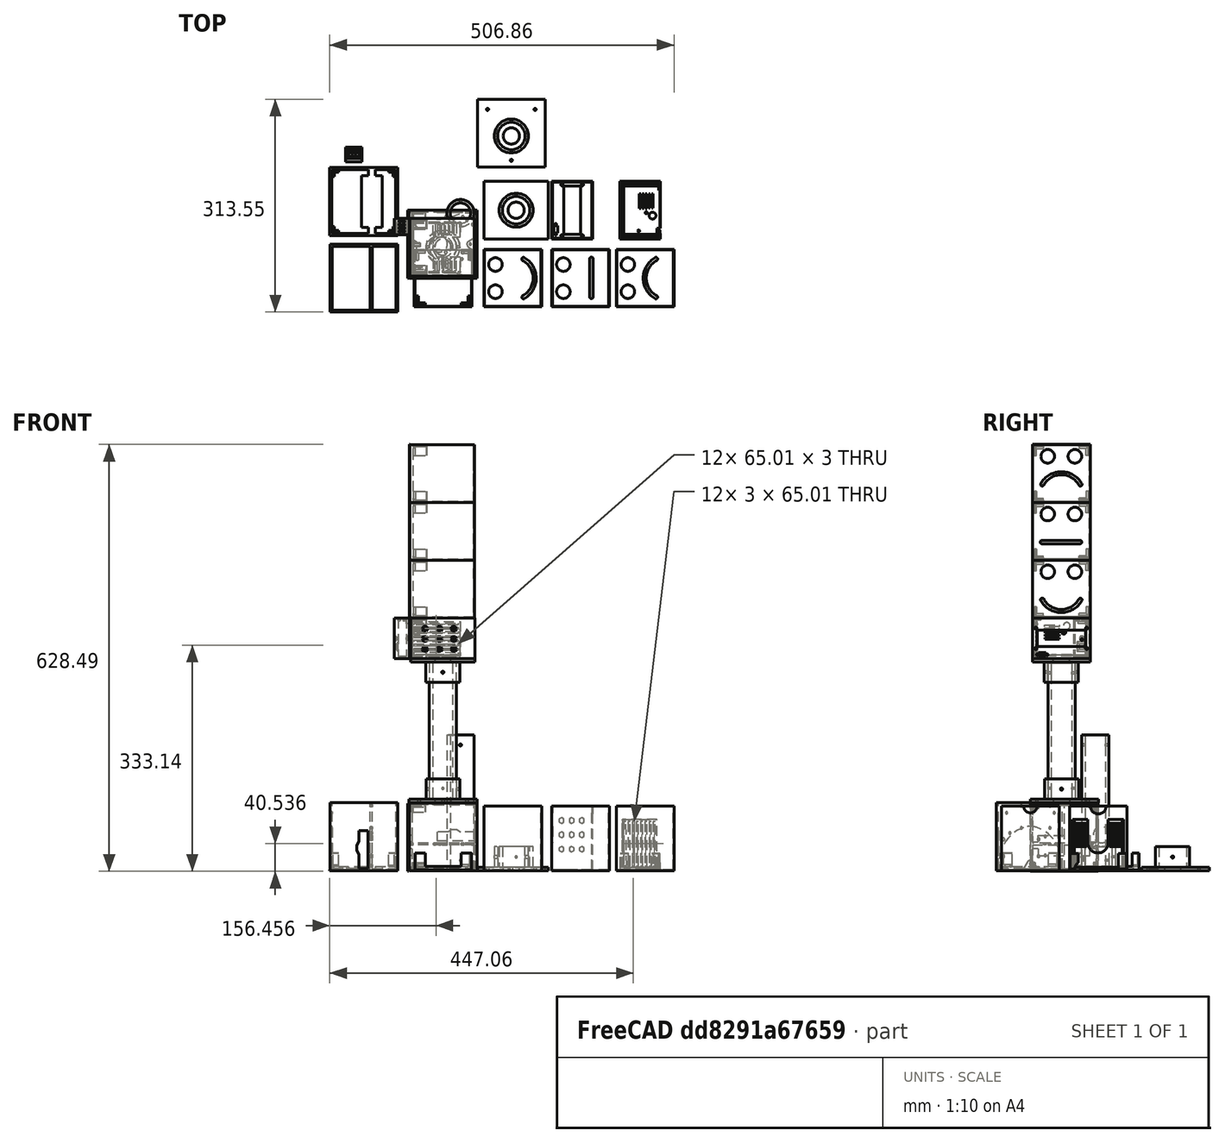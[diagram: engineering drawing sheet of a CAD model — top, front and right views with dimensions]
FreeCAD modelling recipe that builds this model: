
FCSTD DOCUMENT  (FreeCAD 0.18.4R)
Label: design
License: All rights reserved
LicenseURL: http://en.wikipedia.org/wiki/All_rights_reserved
objects: Sketcher::SketchObject×59, PartDesign::Pad×30, PartDesign::Pocket×29, Part::FeaturePython×16, PartDesign::Body×14, Mesh::Feature×4, PartDesign::Chamfer×3, PartDesign::Plane×3, App::DocumentObjectGroup×3, PartDesign::Mirrored×1, PartDesign::Fillet×1, PartDesign::LinearPattern×1
note: 216 computed .brp shape members not serialized (recipe doc carries the construction recipe); baked Part::Feature solids carry a one-line shape summary decoded from their .brp

FEATURE [Sketcher::SketchObject] Sketch
  MapMode = 5
  Support = -> [XY_Plane]
  sketch-geometry (4):
    g0: LineSegment StartX=-42.45 StartY=42.45 StartZ=0 EndX=42.45 EndY=42.45 EndZ=0
    g1: LineSegment StartX=42.45 StartY=42.45 StartZ=0 EndX=42.45 EndY=-42.45 EndZ=0
    g2: LineSegment StartX=42.45 StartY=-42.45 StartZ=0 EndX=-42.45 EndY=-42.45 EndZ=0
    g3: LineSegment StartX=-42.45 StartY=-42.45 StartZ=0 EndX=-42.45 EndY=42.45 EndZ=0
  constraints (11):
    c: Coincident(g0,g1)
    c: Coincident(g1,g2)
    c: Coincident(g2,g3)
    c: Coincident(g3,g0)
    c: Horizontal(g0)
    c: Horizontal(g2)
    c: Vertical(g1)
    c: Vertical(g3)
    c: Symmetric(g0,g1,g-1)
    c: DistanceX(g0,g0) = 84.9
    c: Equal(g0,g1)
FEATURE [PartDesign::Pad] Pad
  Length = 1
  Length2 = 100
  Profile = -> Sketch
  Refine = true
  Type = 0
FEATURE [Sketcher::SketchObject] Sketch001
  ExternalGeometry = -> [Pad]
  MapMode = 5
  Placement = pos=(0,0,1) rot=(0,0,1;0rad)
  Support = -> [Pad]
  sketch-geometry (4):
    g0: LineSegment StartX=-41.45 StartY=41.45 StartZ=0 EndX=41.45 EndY=41.45 EndZ=0
    g1: LineSegment StartX=41.45 StartY=41.45 StartZ=0 EndX=41.45 EndY=-41.45 EndZ=0
    g2: LineSegment StartX=41.45 StartY=-41.45 StartZ=0 EndX=-41.45 EndY=-41.45 EndZ=0
    g3: LineSegment StartX=-41.45 StartY=-41.45 StartZ=0 EndX=-41.45 EndY=41.45 EndZ=0
  constraints (11):
    c: Coincident(g0,g1)
    c: Coincident(g1,g2)
    c: Coincident(g2,g3)
    c: Coincident(g3,g0)
    c: Horizontal(g0)
    c: Horizontal(g2)
    c: Vertical(g1)
    c: Vertical(g3)
    c: Symmetric(g1,g0,g-1)
    c: DistanceX(g-4,g0) = 1
    c: DistanceY(g0,g-4) = 1
FEATURE [PartDesign::Pad] Pad001
  BaseFeature = -> Pad
  Length = 5
  Length2 = 100
  Profile = -> Sketch001
  Refine = true
  Type = 0
FEATURE [Sketcher::SketchObject] Sketch002
  ExternalGeometry = -> [Pad001]
  MapMode = 5
  Placement = pos=(0,0,6) rot=(0,0,1;0rad)
  Support = -> [Pad001]
  sketch-geometry (12):
    g0: LineSegment StartX=-26.45 StartY=41.45 StartZ=0 EndX=-26.45 EndY=39.45 EndZ=0
    g1: LineSegment StartX=-26.45 StartY=39.45 StartZ=0 EndX=-39.45 EndY=39.45 EndZ=0
    g2: LineSegment StartX=-41.45 StartY=41.45 StartZ=0 EndX=-26.45 EndY=41.45 EndZ=0
    g3: LineSegment StartX=-39.45 StartY=39.45 StartZ=0 EndX=-39.45 EndY=26.45 EndZ=0
    g4: LineSegment StartX=-39.45 StartY=26.45 StartZ=0 EndX=-41.45 EndY=26.45 EndZ=0
    g5: LineSegment StartX=-41.45 StartY=26.45 StartZ=0 EndX=-41.45 EndY=41.45 EndZ=0
    g6: LineSegment StartX=26.45 StartY=41.45 StartZ=0 EndX=26.45 EndY=39.45 EndZ=0
    g7: LineSegment StartX=26.45 StartY=39.45 StartZ=0 EndX=39.45 EndY=39.45 EndZ=0
    g8: LineSegment StartX=41.45 StartY=41.45 StartZ=0 EndX=26.45 EndY=41.45 EndZ=0
    g9: LineSegment StartX=39.45 StartY=39.45 StartZ=0 EndX=39.45 EndY=26.45 EndZ=0
    g10: LineSegment StartX=39.45 StartY=26.45 StartZ=0 EndX=41.45 EndY=26.45 EndZ=0
    g11: LineSegment StartX=41.45 StartY=26.45 StartZ=0 EndX=41.45 EndY=41.45 EndZ=0
  constraints (34):
    c: Coincident(g0,g1)
    c: Horizontal(g1)
    c: Vertical(g0)
    c: Coincident(g3,g4)
    c: Coincident(g4,g5)
    c: Coincident(g5,g2)
    c: Horizontal(g2)
    c: Horizontal(g4)
    c: Vertical(g3)
    c: Vertical(g5)
    c: Coincident(g1,g3)
    c: Coincident(g2,g0)
    c: Coincident(g2,g-4)
    c: Equal(g0,g4)
    c: DistanceY(g0,g0) = 2
    c: Equal(g3,g1)
    c: DistanceY(g3,g3) = 13
    c: Coincident(g6,g7)
    c: Horizontal(g7)
    c: Vertical(g6)
    c: Coincident(g9,g10)
    c: Coincident(g10,g11)
    c: Coincident(g11,g8)
    c: Horizontal(g8)
    c: Horizontal(g10)
    c: Vertical(g9)
    c: Vertical(g11)
    c: Coincident(g7,g9)
    c: Coincident(g6,g8)
    c: Equal(g10,g6)
    c: Equal(g6,g0)
    c: Coincident(g8,g-6)
    c: Equal(g9,g7)
    c: Equal(g7,g1)
FEATURE [PartDesign::Pad] Pad002
  BaseFeature = -> Pad001
  Length = 20
  Length2 = 100
  Profile = -> Sketch002
  Refine = true
  Type = 0
FEATURE [PartDesign::Mirrored] Mirrored
  BaseFeature = -> Pad002
  MirrorPlane = -> Sketch002 [H_Axis]
  Originals = -> [Pad002]
  Refine = true
FEATURE [PartDesign::Fillet] Fillet
  Base = -> Mirrored [Edge84,Edge83,Edge23,Edge17]
  BaseFeature = -> Mirrored
  Radius = 1
FEATURE [PartDesign::Chamfer] Chamfer
  Base = -> Fillet [Edge63,Edge64,Edge59,Edge60,Edge72,Edge71,Edge68,Edge67]
  BaseFeature = -> Fillet
  Size = 3
FEATURE [PartDesign::Body] Body  label="tapa-posterior"
  Group = -> [Sketch,Pad,Sketch001,Pad001,Sketch002,Pad002,Mirrored,Fillet,Chamfer]
  Origin = -> Origin
  Tip = -> Chamfer
FEATURE [Sketcher::SketchObject] Sketch003
  MapMode = 5
  Support = -> [XY_Plane001]
  sketch-geometry (10):
    g0: LineSegment StartX=60 StartY=42.45 StartZ=0 EndX=144.9 EndY=42.45 EndZ=0
    g1: LineSegment StartX=144.9 StartY=42.45 StartZ=0 EndX=144.97 EndY=-42.45 EndZ=0
    g2: LineSegment StartX=144.97 StartY=-42.45 StartZ=0 EndX=60 EndY=-42.45 EndZ=0
    g3: LineSegment StartX=60 StartY=-42.45 StartZ=0 EndX=60 EndY=42.45 EndZ=0
    g4: Circle CenterX=77 CenterY=20 CenterZ=0 NormalX=0 NormalY=0 NormalZ=1 AngleXU=0 Radius=10
    g5: Circle CenterX=77 CenterY=-20 CenterZ=0 NormalX=0 NormalY=0 NormalZ=1 AngleXU=0 Radius=10
    g6: ArcOfCircle CenterX=103.039 CenterY=0 CenterZ=0 NormalX=0 NormalY=0 NormalZ=1 AngleXU=0 Radius=29.5 StartAngle=5.20877 EndAngle=7.36453
    g7: ArcOfCircle CenterX=101.991 CenterY=-0.0129152 CenterZ=0 NormalX=0 NormalY=0 NormalZ=1 AngleXU=0 Radius=35 StartAngle=5.23727 EndAngle=7.33604
    g8: ArcOfCircle CenterX=118.3 CenterY=28.1135 CenterZ=0 NormalX=0 NormalY=0 NormalZ=1 AngleXU=0 Radius=2.5 StartAngle=1.15101 EndAngle=4.12215
    g9: ArcOfCircle CenterX=118.37 CenterY=-28.0865 CenterZ=0 NormalX=0 NormalY=0 NormalZ=1 AngleXU=0 Radius=2.5 StartAngle=2.10877 EndAngle=5.19473
  constraints (27):
    c: Coincident(g1,g2)
    c: Coincident(g2,g3)
    c: Coincident(g3,g0)
    c: Horizontal(g0)
    c: Horizontal(g2)
    c: Equal(g0,g3)
    c: DistanceY(g1,g1) = 84.9
    c: Symmetric(g2,g0,g-1)
    c: DistanceX(g-1,g2) = 60
    c: Equal(g5,g4)
    c: Radius(g4) = 10
    c: Symmetric(g4,g5,g-1)
    c: DistanceX(g0,g4) = 17
    c: DistanceY(g5,g4) = 40
    c: PointOnObject(g6,g-1)
    c: Radius(g8) = 2.5
    c: Equal(g9,g8)
    c: DistanceX(g9,g1) = 26.6
    c: DistanceX(g8,g0) = 26.6
    c: DistanceY(g9,g8) = 56.2
    c: Coincident(g9,g6)
    c: Coincident(g9,g7)
    c: Coincident(g8,g7)
    c: Coincident(g8,g6)
    c: Radius(g6) = 29.5
    c: Radius(g7) = 35
    c: Coincident(g0,g1)
FEATURE [PartDesign::Pad] Pad003
  Length = 1
  Length2 = 100
  Profile = -> Sketch003
  Refine = true
  Type = 0
FEATURE [Sketcher::SketchObject] Sketch004
  ExternalGeometry = -> [Pad003]
  MapMode = 5
  Placement = pos=(0,0,1) rot=(0,0,1;0rad)
  Support = -> [Pad003]
  sketch-geometry (8):
    g0: LineSegment StartX=60 StartY=42.45 StartZ=0 EndX=144.97 EndY=42.45 EndZ=0
    g1: LineSegment StartX=144.97 StartY=42.45 StartZ=0 EndX=144.97 EndY=-42.45 EndZ=0
    g2: LineSegment StartX=144.97 StartY=-42.45 StartZ=0 EndX=60 EndY=-42.45 EndZ=0
    g3: LineSegment StartX=60 StartY=-42.45 StartZ=0 EndX=60 EndY=42.45 EndZ=0
    g4: LineSegment StartX=61 StartY=41.4849 StartZ=0 EndX=143.97 EndY=41.4849 EndZ=0
    g5: LineSegment StartX=143.97 StartY=41.4849 StartZ=0 EndX=143.97 EndY=-41.4849 EndZ=0
    g6: LineSegment StartX=143.97 StartY=-41.4849 StartZ=0 EndX=61 EndY=-41.4849 EndZ=0
    g7: LineSegment StartX=61 StartY=-41.4849 StartZ=0 EndX=61 EndY=41.4849 EndZ=0
  constraints (21):
    c: Coincident(g0,g1)
    c: Coincident(g1,g2)
    c: Coincident(g2,g3)
    c: Coincident(g3,g0)
    c: Horizontal(g0)
    c: Horizontal(g2)
    c: Vertical(g1)
    c: Vertical(g3)
    c: Coincident(g0,g-4)
    c: Coincident(g1,g-6)
    c: Coincident(g4,g5)
    c: Coincident(g5,g6)
    c: Coincident(g6,g7)
    c: Coincident(g7,g4)
    c: Horizontal(g4)
    c: Horizontal(g6)
    c: Vertical(g5)
    c: Symmetric(g4,g6,g-1)
    c: Equal(g7,g4)
    c: DistanceX(g4,g0) = 1
    c: DistanceX(g0,g4) = 1
FEATURE [PartDesign::Pad] Pad004
  BaseFeature = -> Pad003
  Length = 94
  Length2 = 100
  Profile = -> Sketch004
  Refine = true
  Type = 0
FEATURE [Sketcher::SketchObject] Sketch005
  ExternalGeometry = -> [Pad004]
  MapMode = 5
  Placement = pos=(144.97,0,0) rot=(0.57735,0.57735,0.57735;2.0944rad)
  Support = -> [Pad004]
  sketch-geometry (1):
    g0: Circle CenterX=0 CenterY=95 CenterZ=0 NormalX=0 NormalY=0 NormalZ=1 AngleXU=0 Radius=10
  constraints (3):
    c: PointOnObject(g0,g-2)
    c: PointOnObject(g0,g-3)
    c: Radius(g0) = 10
FEATURE [PartDesign::Pocket] Pocket
  BaseFeature = -> Pad004
  Length = 5
  Length2 = 100
  Profile = -> Sketch005
  Refine = true
  Type = 1
FEATURE [PartDesign::Body] Body001  label="verde"
  Group = -> [Sketch003,Pad003,Sketch004,Pad004,Sketch005,Pocket]
  Origin = -> Origin001
  Tip = -> Pocket
FEATURE [Sketcher::SketchObject] Sketch006
  AttachmentOffset = pos=(100,0,0) rot=(0,0,1;0rad)
  MapMode = 5
  Placement = pos=(100,0,0) rot=(0,0,1;0rad)
  Support = -> [XY_Plane002]
  sketch-geometry (12):
    g0: LineSegment StartX=60 StartY=42.45 StartZ=0 EndX=144.9 EndY=42.45 EndZ=0
    g1: LineSegment StartX=144.9 StartY=42.45 StartZ=0 EndX=144.9 EndY=-42.45 EndZ=0
    g2: LineSegment StartX=144.9 StartY=-42.45 StartZ=0 EndX=60 EndY=-42.45 EndZ=0
    g3: LineSegment StartX=60 StartY=-42.45 StartZ=0 EndX=60 EndY=42.45 EndZ=0
    g4: Circle CenterX=77 CenterY=20 CenterZ=0 NormalX=0 NormalY=0 NormalZ=1 AngleXU=0 Radius=10
    g5: Circle CenterX=77 CenterY=-20 CenterZ=0 NormalX=0 NormalY=0 NormalZ=1 AngleXU=0 Radius=10
    g6: ArcOfCircle CenterX=118.3 CenterY=28.45 CenterZ=0 NormalX=0 NormalY=0 NormalZ=1 AngleXU=0 Radius=2.5 StartAngle=6.2e-15 EndAngle=3.14159
    g7: ArcOfCircle CenterX=118.3 CenterY=-27.75 CenterZ=0 NormalX=0 NormalY=0 NormalZ=1 AngleXU=0 Radius=2.5 StartAngle=3.14159 EndAngle=6.28319
    g8: LineSegment StartX=115.8 StartY=28.45 StartZ=0 EndX=115.8 EndY=-27.75 EndZ=0
    g9: LineSegment StartX=120.8 StartY=28.45 StartZ=0 EndX=120.8 EndY=-27.75 EndZ=0
    g10: LineSegment [constr] StartX=114.062 StartY=-27.75 StartZ=0 EndX=122.672 EndY=-27.75 EndZ=0
    g11: LineSegment [constr] StartX=113.721 StartY=28.45 StartZ=0 EndX=123.058 EndY=28.45 EndZ=0
  constraints (35):
    c: Coincident(g1,g2)
    c: Coincident(g2,g3)
    c: Coincident(g3,g0)
    c: Horizontal(g0)
    c: Horizontal(g2)
    c: Equal(g0,g3)
    c: DistanceY(g1,g1) = 84.9
    c: Symmetric(g2,g0,g-1)
    c: DistanceX(g-1,g2) = 60
    c: Equal(g5,g4)
    c: Radius(g4) = 10
    c: Symmetric(g4,g5,g-1)
    c: DistanceX(g0,g4) = 17
    c: DistanceY(g5,g4) = 40
    c: Radius(g6) = 2.5
    c: Equal(g7,g6)
    c: DistanceX(g7,g1) = 26.6
    c: DistanceX(g6,g0) = 26.6
    c: DistanceY(g7,g6) = 56.2
    c: Coincident(g0,g1)
    c: Vertical(g8)
    c: Tangent(g9,g7) = 1.5708
    c: Coincident(g6,g8)
    c: Coincident(g6,g9)
    c: Coincident(g7,g8)
    c: Coincident(g7,g9)
    c: Parallel(g8,g9)
    c: DistanceY(g6,g0) = 14
    c: Horizontal(g10)
    c: PointOnObject(g7,g10)
    c: PointOnObject(g7,g10)
    c: Horizontal(g11)
    c: PointOnObject(g6,g11)
    c: PointOnObject(g6,g11)
    c: PointOnObject(g6,g11)
FEATURE [PartDesign::Pad] Pad005
  Length = 1
  Length2 = 100
  Profile = -> Sketch006
  Refine = true
  Type = 0
FEATURE [Sketcher::SketchObject] Sketch007
  ExternalGeometry = -> [Pad005]
  MapMode = 5
  Placement = pos=(0,0,1) rot=(0,0,1;0rad)
  Support = -> [Pad005]
  sketch-geometry (8):
    g0: LineSegment StartX=160 StartY=42.45 StartZ=0 EndX=244.9 EndY=42.45 EndZ=0
    g1: LineSegment StartX=244.9 StartY=42.45 StartZ=0 EndX=244.9 EndY=-42.45 EndZ=0
    g2: LineSegment StartX=244.9 StartY=-42.45 StartZ=0 EndX=160 EndY=-42.45 EndZ=0
    g3: LineSegment StartX=160 StartY=-42.45 StartZ=0 EndX=160 EndY=42.45 EndZ=0
    g4: LineSegment StartX=161 StartY=41.45 StartZ=0 EndX=243.9 EndY=41.45 EndZ=0
    g5: LineSegment StartX=243.9 StartY=41.45 StartZ=0 EndX=243.9 EndY=-41.45 EndZ=0
    g6: LineSegment StartX=243.9 StartY=-41.45 StartZ=0 EndX=161 EndY=-41.45 EndZ=0
    g7: LineSegment StartX=161 StartY=-41.45 StartZ=0 EndX=161 EndY=41.45 EndZ=0
  constraints (21):
    c: Coincident(g0,g1)
    c: Coincident(g1,g2)
    c: Coincident(g2,g3)
    c: Coincident(g3,g0)
    c: Horizontal(g0)
    c: Horizontal(g2)
    c: Vertical(g1)
    c: Vertical(g3)
    c: Coincident(g0,g-3)
    c: Coincident(g1,g-4)
    c: Coincident(g4,g5)
    c: Coincident(g5,g6)
    c: Coincident(g6,g7)
    c: Coincident(g7,g4)
    c: Horizontal(g4)
    c: Horizontal(g6)
    c: Vertical(g5)
    c: Equal(g7,g4)
    c: Symmetric(g4,g6,g-1)
    c: DistanceX(g4,g0) = 1
    c: DistanceX(g0,g4) = 1
FEATURE [PartDesign::Pad] Pad006
  BaseFeature = -> Pad005
  Length = 94
  Length2 = 1
  Profile = -> Sketch007
  Refine = true
  Type = 0
FEATURE [Sketcher::SketchObject] Sketch008
  ExternalGeometry = -> [Pad006]
  MapMode = 5
  Placement = pos=(244.9,0,0) rot=(0.57735,0.57735,0.57735;2.0944rad)
  Support = -> [Pad006]
  sketch-geometry (1):
    g0: Circle CenterX=0 CenterY=95 CenterZ=0 NormalX=0 NormalY=0 NormalZ=1 AngleXU=0 Radius=10
  constraints (3):
    c: PointOnObject(g0,g-3)
    c: PointOnObject(g0,g-2)
    c: Radius(g0) = 10
FEATURE [PartDesign::Pocket] Pocket001
  BaseFeature = -> Pad006
  Length = 5
  Length2 = 100
  Profile = -> Sketch008
  Refine = true
  Type = 1
FEATURE [PartDesign::Body] Body002  label="Amarillo"
  Group = -> [Sketch006,Pad005,Sketch007,Pad006,Sketch008,Pocket001]
  Origin = -> Origin002
  Tip = -> Pocket001
FEATURE [Sketcher::SketchObject] Sketch009
  AttachmentOffset = pos=(195,0,0) rot=(0,0,1;0rad)
  MapMode = 5
  Placement = pos=(195,0,0) rot=(0,0,1;0rad)
  Support = -> [XY_Plane003]
  sketch-geometry (11):
    g0: LineSegment StartX=60 StartY=42.45 StartZ=0 EndX=144.9 EndY=42.45 EndZ=0
    g1: LineSegment StartX=144.9 StartY=42.45 StartZ=0 EndX=144.9 EndY=-42.45 EndZ=0
    g2: LineSegment StartX=144.9 StartY=-42.45 StartZ=0 EndX=60 EndY=-42.45 EndZ=0
    g3: LineSegment StartX=60 StartY=-42.45 StartZ=0 EndX=60 EndY=42.45 EndZ=0
    g4: Circle CenterX=77 CenterY=20 CenterZ=0 NormalX=0 NormalY=0 NormalZ=1 AngleXU=0 Radius=10
    g5: Circle CenterX=77 CenterY=-20 CenterZ=0 NormalX=0 NormalY=0 NormalZ=1 AngleXU=0 Radius=10
    g6: LineSegment [constr] StartX=118.3 StartY=28.0937 StartZ=0 EndX=118.3 EndY=-28.1063 EndZ=0
    g7: ArcOfCircle CenterX=118.3 CenterY=28.0937 CenterZ=0 NormalX=0 NormalY=0 NormalZ=1 AngleXU=0 Radius=2.5 StartAngle=5.30178 EndAngle=8.27455
    g8: ArcOfCircle CenterX=134.642 CenterY=-0.013752 CenterZ=0 NormalX=0 NormalY=0 NormalZ=1 AngleXU=0 Radius=35 StartAngle=2.08988 EndAngle=4.18642
    g9: ArcOfCircle CenterX=118.3 CenterY=-28.1063 CenterZ=0 NormalX=0 NormalY=0 NormalZ=1 AngleXU=0 Radius=2.5 StartAngle=4.19823 EndAngle=7.34825
    g10: ArcOfCircle CenterX=133.598 CenterY=0 CenterZ=0 NormalX=0 NormalY=0 NormalZ=1 AngleXU=0 Radius=29.5 StartAngle=2.06176 EndAngle=4.21456
  constraints (24):
    c: Coincident(g1,g2)
    c: Coincident(g2,g3)
    c: Coincident(g3,g0)
    c: Horizontal(g0)
    c: Horizontal(g2)
    c: Equal(g0,g3)
    c: DistanceY(g1,g1) = 84.9
    c: Symmetric(g2,g0,g-1)
    c: DistanceX(g-1,g2) = 60
    c: Equal(g5,g4)
    c: Radius(g4) = 10
    c: Symmetric(g4,g5,g-1)
    c: DistanceX(g0,g4) = 17
    c: DistanceY(g5,g4) = 40
    c: Coincident(g0,g1)
    c: Vertical(g6)
    c: Radius(g7) = 2.5
    c: Equal(g9,g7)
    c: Coincident(g9,g10)
    c: Coincident(g9,g8)
    c: Coincident(g7,g8)
    c: Coincident(g7,g10)
    c: Radius(g10) = 29.5
    c: Radius(g8) = 35
FEATURE [PartDesign::Pad] Pad007
  Length = 1
  Length2 = 100
  Profile = -> Sketch009
  Refine = true
  Type = 0
FEATURE [Sketcher::SketchObject] Sketch010
  ExternalGeometry = -> [Pad007]
  MapMode = 5
  Placement = pos=(0,0,1) rot=(0,0,1;0rad)
  Support = -> [Pad007]
  sketch-geometry (8):
    g0: LineSegment StartX=255 StartY=42.45 StartZ=0 EndX=339.9 EndY=42.45 EndZ=0
    g1: LineSegment StartX=339.9 StartY=42.45 StartZ=0 EndX=339.9 EndY=-42.45 EndZ=0
    g2: LineSegment StartX=339.9 StartY=-42.45 StartZ=0 EndX=255 EndY=-42.45 EndZ=0
    g3: LineSegment StartX=255 StartY=-42.45 StartZ=0 EndX=255 EndY=42.45 EndZ=0
    g4: LineSegment StartX=256 StartY=41.45 StartZ=0 EndX=338.9 EndY=41.45 EndZ=0
    g5: LineSegment StartX=338.9 StartY=41.45 StartZ=0 EndX=338.9 EndY=-41.45 EndZ=0
    g6: LineSegment StartX=338.9 StartY=-41.45 StartZ=0 EndX=256 EndY=-41.45 EndZ=0
    g7: LineSegment StartX=256 StartY=-41.45 StartZ=0 EndX=256 EndY=41.45 EndZ=0
  constraints (21):
    c: Coincident(g0,g1)
    c: Coincident(g1,g2)
    c: Coincident(g2,g3)
    c: Coincident(g3,g0)
    c: Horizontal(g0)
    c: Horizontal(g2)
    c: Vertical(g1)
    c: Vertical(g3)
    c: Coincident(g0,g-3)
    c: Coincident(g1,g-4)
    c: Coincident(g4,g5)
    c: Coincident(g5,g6)
    c: Coincident(g6,g7)
    c: Coincident(g7,g4)
    c: Horizontal(g4)
    c: Horizontal(g6)
    c: Vertical(g5)
    c: Equal(g7,g4)
    c: Symmetric(g4,g6,g-1)
    c: DistanceX(g4,g0) = 1
    c: DistanceX(g0,g4) = 1
FEATURE [PartDesign::Pad] Pad008
  BaseFeature = -> Pad007
  Length = 94
  Length2 = 100
  Profile = -> Sketch010
  Refine = true
  Type = 0
FEATURE [Sketcher::SketchObject] Sketch011
  ExternalGeometry = -> [Pad008]
  MapMode = 5
  Placement = pos=(339.9,0,0) rot=(0.57735,0.57735,0.57735;2.0944rad)
  Support = -> [Pad008]
  sketch-geometry (1):
    g0: Circle CenterX=0 CenterY=95 CenterZ=0 NormalX=0 NormalY=0 NormalZ=1 AngleXU=0 Radius=10
  constraints (3):
    c: PointOnObject(g0,g-3)
    c: PointOnObject(g0,g-2)
    c: Radius(g0) = 10
FEATURE [PartDesign::Pocket] Pocket002
  BaseFeature = -> Pad008
  Length = 5
  Length2 = 100
  Profile = -> Sketch011
  Refine = true
  Type = 0
FEATURE [PartDesign::Body] Body003  label="Rojo"
  Group = -> [Sketch009,Pad007,Sketch010,Pad008,Sketch011,Pocket002]
  Origin = -> Origin003
  Tip = -> Pocket002
FEATURE [Sketcher::SketchObject] Sketch012
  AttachmentOffset = pos=(0,100,0) rot=(0,0,1;0rad)
  MapMode = 5
  Placement = pos=(0,100,0) rot=(0,0,1;0rad)
  Support = -> [XY_Plane004]
  sketch-geometry (8):
    g0: LineSegment StartX=60 StartY=42.5 StartZ=0 EndX=155 EndY=42.5 EndZ=0
    g1: LineSegment StartX=155 StartY=42.5 StartZ=0 EndX=155 EndY=-42.5 EndZ=0
    g2: LineSegment StartX=155 StartY=-42.5 StartZ=0 EndX=60 EndY=-42.5 EndZ=0
    g3: LineSegment StartX=60 StartY=-42.5 StartZ=0 EndX=60 EndY=42.5 EndZ=0
    g4: Circle CenterX=107.5 CenterY=-2e-15 CenterZ=0 NormalX=0 NormalY=0 NormalZ=1 AngleXU=0 Radius=12
    g5: LineSegment [constr] StartX=60 StartY=-42.5 StartZ=0 EndX=155 EndY=42.5 EndZ=0
    g6: LineSegment [constr] StartX=107.5 StartY=-2e-15 StartZ=0 EndX=155 EndY=-42.5 EndZ=0
    g7: LineSegment [constr] StartX=107.5 StartY=42.5 StartZ=0 EndX=107.5 EndY=-27.435 EndZ=0
  constraints (22):
    c: DistanceY(g1,g1) = 85
    c: Symmetric(g2,g0,g-1)
    c: DistanceX(g-1,g2) = 60
    c: Radius(g4) = 12
    c: Coincident(g5,g2)
    c: Coincident(g5,g0)
    c: PointOnObject(g4,g5)
    c: Coincident(g0,g3)
    c: Coincident(g0,g1)
    c: Coincident(g2,g3)
    c: Coincident(g1,g2)
    c: Horizontal(g0)
    c: Horizontal(g2)
    c: Vertical(g1)
    c: DistanceX(g0,g0) = 95
    c: Coincident(g6,g1)
    c: Distance(g6,g0) = 63.7377
    c: Coincident(g4,g6)
    c: PointOnObject(g7,g0)
    c: Vertical(g7)
    c: DistanceX(g7,g0) = 47.5
    c: PointOnObject(g4,g7)
FEATURE [PartDesign::Pad] Pad009
  Length = 5
  Length2 = 100
  Profile = -> Sketch012
  Refine = true
  Type = 0
FEATURE [Sketcher::SketchObject] Sketch013
  ExternalGeometry = -> [Pad009]
  MapMode = 5
  Placement = pos=(0,0,5) rot=(0,0,1;0rad)
  Support = -> [Pad009]
  sketch-geometry (3):
    g0: Circle CenterX=107.5 CenterY=100 CenterZ=0 NormalX=0 NormalY=0 NormalZ=1 AngleXU=0 Radius=20.25
    g1: Circle [constr] CenterX=107.5 CenterY=100 CenterZ=0 NormalX=0 NormalY=0 NormalZ=1 AngleXU=0 Radius=20
    g2: Circle CenterX=107.5 CenterY=100 CenterZ=0 NormalX=0 NormalY=0 NormalZ=1 AngleXU=0 Radius=25
  constraints (6):
    c: Coincident(g0,g-3)
    c: Diameter(g0) = 40.5
    c: Coincident(g1,g0)
    c: Diameter(g1) = 40
    c: Coincident(g2,g0)
    c: Diameter(g2) = 50
FEATURE [PartDesign::Pad] Pad010
  BaseFeature = -> Pad009
  Length = 30
  Length2 = 100
  Profile = -> Sketch013
  Refine = true
  Type = 0
FEATURE [PartDesign::Plane] DatumPlane
  AttachmentOffset = pos=(0,-30,0) rot=(1,0,0;1.5708rad)
  Length = 182.234
  MapMode = 45
  Placement = pos=(107.5,70,20) rot=(1,0,0;1.5708rad)
  ResizeMode = 0
  Support = -> [Pad010]
  Width = 62.2337
FEATURE [Sketcher::SketchObject] Sketch014
  MapMode = 5
  Placement = pos=(107.5,70,20) rot=(1,0,0;1.5708rad)
  Support = -> [DatumPlane]
  sketch-geometry (1):
    g0: Circle CenterX=0 CenterY=0 CenterZ=0 NormalX=0 NormalY=0 NormalZ=1 AngleXU=0 Radius=1.5
  constraints (2):
    c: Coincident(g0,g-1)
    c: Diameter(g0) = 3
FEATURE [PartDesign::Pocket] Pocket003
  BaseFeature = -> Pad010
  Length = 5
  Length2 = 100
  Profile = -> Sketch014
  Refine = true
  Type = 1
FEATURE [PartDesign::Body] Body004  label="soporte-tubo-superior"
  Group = -> [Sketch012,Pad009,Sketch013,Pad010,DatumPlane,Sketch014,Pocket003]
  Origin = -> Origin004
  Tip = -> Pocket003
FEATURE [Sketcher::SketchObject] Sketch015
  AttachmentOffset = pos=(100,100,0) rot=(0,0,1;0rad)
  MapMode = 5
  Placement = pos=(100,100,0) rot=(0,0,1;0rad)
  Support = -> [XY_Plane005]
  sketch-geometry (4):
    g0: LineSegment StartX=60 StartY=42.45 StartZ=0 EndX=120 EndY=42.45 EndZ=0
    g1: LineSegment StartX=120 StartY=42.45 StartZ=0 EndX=120 EndY=-42.45 EndZ=0
    g2: LineSegment StartX=120 StartY=-42.45 StartZ=0 EndX=60 EndY=-42.45 EndZ=0
    g3: LineSegment StartX=60 StartY=-42.45 StartZ=0 EndX=60 EndY=42.45 EndZ=0
  constraints (11):
    c: Coincident(g1,g2)
    c: Coincident(g2,g3)
    c: Coincident(g3,g0)
    c: Horizontal(g0)
    c: Horizontal(g2)
    c: DistanceY(g1,g1) = 84.9
    c: Symmetric(g2,g0,g-1)
    c: DistanceX(g-1,g2) = 60
    c: Coincident(g0,g1)
    c: DistanceX(g0,g0) = 60
    c: Equal(g2,g0)
FEATURE [PartDesign::Pad] Pad011
  Length = 1
  Length2 = 100
  Profile = -> Sketch015
  Refine = true
  Type = 0
FEATURE [Sketcher::SketchObject] Sketch016
  ExternalGeometry = -> [Pad011]
  MapMode = 5
  Placement = pos=(0,0,1) rot=(0,0,1;0rad)
  Support = -> [Pad011]
  sketch-geometry (8):
    g0: LineSegment StartX=160 StartY=142.45 StartZ=0 EndX=220 EndY=142.45 EndZ=0
    g1: LineSegment StartX=220 StartY=142.45 StartZ=0 EndX=220 EndY=57.55 EndZ=0
    g2: LineSegment StartX=220 StartY=57.55 StartZ=0 EndX=160 EndY=57.55 EndZ=0
    g3: LineSegment StartX=160 StartY=57.55 StartZ=0 EndX=160 EndY=142.45 EndZ=0
    g4: LineSegment StartX=161 StartY=141.45 StartZ=0 EndX=219 EndY=141.45 EndZ=0
    g5: LineSegment StartX=219 StartY=141.45 StartZ=0 EndX=219 EndY=58.55 EndZ=0
    g6: LineSegment StartX=219 StartY=58.55 StartZ=0 EndX=161 EndY=58.55 EndZ=0
    g7: LineSegment StartX=161 StartY=58.55 StartZ=0 EndX=161 EndY=141.45 EndZ=0
  constraints (22):
    c: Coincident(g0,g1)
    c: Coincident(g1,g2)
    c: Coincident(g2,g3)
    c: Coincident(g3,g0)
    c: Horizontal(g0)
    c: Horizontal(g2)
    c: Vertical(g1)
    c: Vertical(g3)
    c: Coincident(g0,g-3)
    c: Coincident(g1,g-4)
    c: Coincident(g4,g5)
    c: Coincident(g5,g6)
    c: Coincident(g6,g7)
    c: Coincident(g7,g4)
    c: Horizontal(g4)
    c: Horizontal(g6)
    c: Vertical(g5)
    c: Vertical(g7)
    c: DistanceY(g4,g0) = 1
    c: DistanceX(g0,g4) = 1
    c: DistanceY(g2,g6) = 1
    c: DistanceX(g5,g1) = 1
FEATURE [PartDesign::Pad] Pad012
  BaseFeature = -> Pad011
  Length = 94
  Length2 = 100
  Profile = -> Sketch016
  Refine = true
  Type = 0
FEATURE [Sketcher::SketchObject] Sketch017
  ExternalGeometry = -> [Pad012]
  MapMode = 5
  Placement = pos=(160,0,0) rot=(0.57735,-0.57735,-0.57735;2.0944rad)
  Support = -> [Pad012]
  sketch-geometry (3):
    g0: LineSegment [constr] StartX=-142.45 StartY=95 StartZ=0 EndX=-57.55 EndY=0 EndZ=0
    g1: LineSegment [constr] StartX=-57.55 StartY=95 StartZ=0 EndX=-104.752 EndY=52.8168 EndZ=0
    g2: Circle CenterX=-104.752 CenterY=52.8168 CenterZ=0 NormalX=0 NormalY=0 NormalZ=1 AngleXU=0 Radius=12
  constraints (7):
    c: Coincident(g0,g-3)
    c: Coincident(g0,g-4)
    c: Coincident(g1,g-4)
    c: PointOnObject(g1,g0)
    c: Perpendicular(g0,g1)
    c: Coincident(g2,g1)
    c: Diameter(g2) = 24
FEATURE [PartDesign::Pocket] Pocket004
  BaseFeature = -> Pad012
  Length = 5
  Length2 = 100
  Profile = -> Sketch017
  Refine = true
  Type = 0
FEATURE [Sketcher::SketchObject] Sketch018
  ExternalGeometry = -> [Pocket004]
  MapMode = 5
  Placement = pos=(220,0,0) rot=(0.57735,0.57735,0.57735;2.0944rad)
  Support = -> [Pocket004]
  sketch-geometry (1):
    g0: Circle CenterX=100 CenterY=95 CenterZ=0 NormalX=0 NormalY=0 NormalZ=1 AngleXU=0 Radius=11.6839
  constraints (3):
    c: PointOnObject(g0,g-3)
    c: DistanceX(g-3,g-3) = 84.9
    c: DistanceX(g-3,g0) = 42.45
FEATURE [PartDesign::Pocket] Pocket005
  BaseFeature = -> Pocket004
  Length = 5
  Length2 = 100
  Profile = -> Sketch018
  Refine = true
  Type = 0
FEATURE [Sketcher::SketchObject] Sketch019
  ExternalGeometry = -> [Pocket005]
  MapMode = 5
  Placement = pos=(0,0,0) rot=(1,0,0;3.14159rad)
  Support = -> [Pocket005]
  sketch-geometry (23):
    g0: LineSegment [constr] StartX=172 StartY=-60 StartZ=0 EndX=208 EndY=-60 EndZ=0
    g1: LineSegment [constr] StartX=208 StartY=-60 StartZ=0 EndX=208 EndY=-140 EndZ=0
    g2: LineSegment [constr] StartX=208 StartY=-140 StartZ=0 EndX=172 EndY=-140 EndZ=0
    g3: LineSegment [constr] StartX=172 StartY=-140 StartZ=0 EndX=172 EndY=-60 EndZ=0
    g4: LineSegment [constr] StartX=175 StartY=-62.5 StartZ=0 EndX=205 EndY=-62.5 EndZ=0
    g5: LineSegment [constr] StartX=205 StartY=-62.5 StartZ=0 EndX=205 EndY=-137.5 EndZ=0
    g6: LineSegment [constr] StartX=205 StartY=-137.5 StartZ=0 EndX=175 EndY=-137.5 EndZ=0
    g7: LineSegment [constr] StartX=175 StartY=-137.5 StartZ=0 EndX=175 EndY=-62.5 EndZ=0
    g8: Circle CenterX=175 CenterY=-137.5 CenterZ=0 NormalX=0 NormalY=0 NormalZ=1 AngleXU=0 Radius=1.6
    g9: Circle CenterX=205 CenterY=-137.5 CenterZ=0 NormalX=0 NormalY=0 NormalZ=1 AngleXU=0 Radius=1.6
    g10: Circle CenterX=175 CenterY=-62.5 CenterZ=0 NormalX=0 NormalY=0 NormalZ=1 AngleXU=0 Radius=1.6
    g11: Circle CenterX=205 CenterY=-62.5 CenterZ=0 NormalX=0 NormalY=0 NormalZ=1 AngleXU=0 Radius=1.6
    g12: LineSegment StartX=177.8 StartY=-64.3 StartZ=0 EndX=202.2 EndY=-64.3 EndZ=0
    g13: LineSegment StartX=202.2 StartY=-64.3 StartZ=0 EndX=202.2 EndY=-135.7 EndZ=0
    g14: LineSegment StartX=202.2 StartY=-135.7 StartZ=0 EndX=177.8 EndY=-135.7 EndZ=0
    g15: LineSegment StartX=177.8 StartY=-135.7 StartZ=0 EndX=177.8 EndY=-64.3 EndZ=0
    g16: LineSegment StartX=163 StartY=-66.5878 StartZ=0 EndX=168.7 EndY=-66.5878 EndZ=0
    g17: LineSegment StartX=168.7 StartY=-66.5878 StartZ=0 EndX=168.7 EndY=-77.2378 EndZ=0
    g18: LineSegment StartX=168.7 StartY=-77.2378 StartZ=0 EndX=163 EndY=-77.2378 EndZ=0
    g19: LineSegment StartX=163 StartY=-77.2378 StartZ=0 EndX=163 EndY=-66.5878 EndZ=0
    g20: LineSegment [constr] StartX=165.85 StartY=-64.4128 StartZ=0 EndX=165.85 EndY=-79.4128 EndZ=0
    g21: Circle CenterX=165.85 CenterY=-64.4128 CenterZ=0 NormalX=0 NormalY=0 NormalZ=1 AngleXU=0 Radius=1.25
    g22: Circle CenterX=165.85 CenterY=-79.4128 CenterZ=0 NormalX=0 NormalY=0 NormalZ=1 AngleXU=0 Radius=1.25
  constraints (65):
    c: Coincident(g0,g1)
    c: Coincident(g1,g2)
    c: Coincident(g2,g3)
    c: Coincident(g3,g0)
    c: Horizontal(g0)
    c: Horizontal(g2)
    c: Vertical(g1)
    c: Vertical(g3)
    c: DistanceX(g0,g0) = 36
    c: DistanceY(g1,g1) = 80
    c: DistanceX(g-3,g-3) = 60
    c: DistanceX(g-4,g0) = 12
    c: DistanceY(g-4,g-4) = 84.9
    c: DistanceY(g-5,g2) = 2.45
    c: Coincident(g4,g5)
    c: Coincident(g5,g6)
    c: Coincident(g6,g7)
    c: Coincident(g7,g4)
    c: Horizontal(g4)
    c: Horizontal(g6)
    c: Vertical(g5)
    c: Vertical(g7)
    c: DistanceX(g4,g4) = 30
    c: DistanceY(g5,g5) = 75
    c: DistanceX(g0,g4) = 3
    c: DistanceY(g2,g6) = 2.5
    c: Coincident(g8,g6)
    c: Coincident(g9,g5)
    c: Coincident(g10,g4)
    c: Coincident(g11,g4)
    c: Equal(g10,g11)
    c: Equal(g11,g8)
    c: Equal(g8,g9)
    c: Diameter(g9) = 3.2
    c: Coincident(g12,g13)
    c: Coincident(g13,g14)
    c: Coincident(g14,g15)
    c: Coincident(g15,g12)
    c: Horizontal(g12)
    c: Horizontal(g14)
    c: Vertical(g13)
    c: Vertical(g15)
    c: DistanceX(g14,g14) = 24.4
    c: DistanceY(g13,g13) = 71.4
    c: DistanceX(g10,g12) = 2.8
    c: DistanceY(g9,g13) = 1.8
    c: Coincident(g16,g17)
    c: Coincident(g17,g18)
    c: Coincident(g18,g19)
    c: Coincident(g19,g16)
    c: Horizontal(g16)
    c: Horizontal(g18)
    c: Vertical(g17)
    c: Vertical(g19)
    c: DistanceX(g18,g18) = 5.7
    c: DistanceY(g19,g19) = 10.65
    c: DistanceX(g-4,g16) = 3
    c: Vertical(g20)
    c: DistanceY(g20,g20) = 15
    c: DistanceX(g20,g16) = 2.85
    c: DistanceY(g20,g18) = 2.175
    c: Coincident(g21,g20)
    c: Coincident(g22,g20)
    c: Diameter(g21) = 2.5
    c: Equal(g21,g22)
FEATURE [PartDesign::Pocket] Pocket006
  BaseFeature = -> Pocket005
  Length = 5
  Length2 = 100
  Profile = -> Sketch019
  Refine = true
  Type = 0
FEATURE [Sketcher::SketchObject] Sketch020
  ExternalGeometry = -> [Pocket006]
  MapMode = 5
  Placement = pos=(0,57.55,0) rot=(1,0,0;1.5708rad)
  Support = -> [Pocket006]
  sketch-geometry (22):
    g0: LineSegment StartX=177.622 StartY=71.75 StartZ=0 EndX=177.622 EndY=75.75 EndZ=0
    g1: LineSegment StartX=177.622 StartY=75.75 StartZ=0 EndX=174.158 EndY=77.75 EndZ=0
    g2: LineSegment StartX=174.158 StartY=77.75 StartZ=0 EndX=170.694 EndY=75.75 EndZ=0
    g3: LineSegment StartX=170.694 StartY=75.75 StartZ=0 EndX=170.694 EndY=71.75 EndZ=0
    g4: LineSegment StartX=170.694 StartY=71.75 StartZ=0 EndX=174.158 EndY=69.75 EndZ=0
    g5: LineSegment StartX=174.158 StartY=69.75 StartZ=0 EndX=177.622 EndY=71.75 EndZ=0
    g6: Circle [constr] CenterX=174.158 CenterY=73.75 CenterZ=0 NormalX=0 NormalY=0 NormalZ=1 AngleXU=0 Radius=4
    g7: LineSegment StartX=192.622 StartY=71.75 StartZ=0 EndX=192.622 EndY=75.75 EndZ=0
    g8: LineSegment StartX=192.622 StartY=75.75 StartZ=0 EndX=189.158 EndY=77.75 EndZ=0
    g9: LineSegment StartX=189.158 StartY=77.75 StartZ=0 EndX=185.694 EndY=75.75 EndZ=0
    g10: LineSegment StartX=185.694 StartY=75.75 StartZ=0 EndX=185.694 EndY=71.75 EndZ=0
    g11: LineSegment StartX=185.694 StartY=71.75 StartZ=0 EndX=189.158 EndY=69.75 EndZ=0
    g12: LineSegment StartX=189.158 StartY=69.75 StartZ=0 EndX=192.622 EndY=71.75 EndZ=0
    g13: Circle [constr] CenterX=189.158 CenterY=73.75 CenterZ=0 NormalX=0 NormalY=0 NormalZ=1 AngleXU=0 Radius=4
    g14: LineSegment StartX=207.622 StartY=71.75 StartZ=0 EndX=207.622 EndY=75.75 EndZ=0
    g15: LineSegment StartX=207.622 StartY=75.75 StartZ=0 EndX=204.158 EndY=77.75 EndZ=0
    g16: LineSegment StartX=204.158 StartY=77.75 StartZ=0 EndX=200.694 EndY=75.75 EndZ=0
    g17: LineSegment StartX=200.694 StartY=75.75 StartZ=0 EndX=200.694 EndY=71.75 EndZ=0
    g18: LineSegment StartX=200.694 StartY=71.75 StartZ=0 EndX=204.158 EndY=69.75 EndZ=0
    g19: LineSegment StartX=204.158 StartY=69.75 StartZ=0 EndX=207.622 EndY=71.75 EndZ=0
    g20: Circle [constr] CenterX=204.158 CenterY=73.75 CenterZ=0 NormalX=0 NormalY=0 NormalZ=1 AngleXU=0 Radius=4
    g21: LineSegment [constr] StartX=174.158 StartY=73.75 StartZ=0 EndX=211.403 EndY=73.75 EndZ=0
  constraints (53):
    c: Coincident(g0,g1)
    c: Coincident(g1,g2)
    c: Coincident(g2,g3)
    c: Coincident(g3,g4)
    c: Coincident(g4,g5)
    c: Coincident(g5,g0)
    c: Equal(g0, g1-g5) x5
    c: PointOnObject(g0,g6)
    c: PointOnObject(g1,g6)
    c: PointOnObject(g2,g6)
    c: PointOnObject(g3,g6)
    c: PointOnObject(g4,g6)
    c: PointOnObject(g5,g6)
    c: Diameter(g6) = 8
    c: Coincident(g7,g8)
    c: Coincident(g8,g9)
    c: Coincident(g9,g10)
    c: Coincident(g10,g11)
    c: Coincident(g11,g12)
    c: Coincident(g12,g7)
    c: Equal(g7, g8-g12) x5
    c: PointOnObject(g7,g13)
    c: PointOnObject(g8,g13)
    c: PointOnObject(g9,g13)
    c: PointOnObject(g10,g13)
    c: PointOnObject(g11,g13)
    c: PointOnObject(g12,g13)
    c: Coincident(g14,g15)
    c: Coincident(g15,g16)
    c: Coincident(g16,g17)
    c: Coincident(g17,g18)
    c: Coincident(g18,g19)
    c: Coincident(g19,g14)
    c: Equal(g14, g15-g19) x5
    c: PointOnObject(g14,g20)
    c: PointOnObject(g15,g20)
    c: PointOnObject(g16,g20)
    c: PointOnObject(g17,g20)
    c: PointOnObject(g18,g20)
    c: PointOnObject(g19,g20)
    c: Equal(g20,g13)
    c: Equal(g13,g6)
    c: DistanceX(g6,g13) = 15
    c: DistanceX(g13,g20) = 15
    c: Coincident(g21,g6)
    c: Horizontal(g21)
    c: PointOnObject(g20,g21)
    c: PointOnObject(g13,g21)
    c: DistanceY(g6,g-3) = 21.25
    c: DistanceY(g-4,g-4) = 95
    c: Vertical(g3)
    c: Vertical(g10)
    c: Vertical(g17)
FEATURE [PartDesign::Pocket] Pocket007  label="linea-maestra-orificios"
  BaseFeature = -> Pocket006
  Length = 5
  Length2 = 100
  Profile = -> Sketch020
  Refine = true
  Type = 1
FEATURE [PartDesign::LinearPattern] LinearPattern
  BaseFeature = -> Pocket007
  Direction = -> Sketch020 [V_Axis]
  Length = 42.25
  Occurrences = 3
  Originals = -> [Pocket007]
  Refine = true
  Reversed = true
FEATURE [PartDesign::Body] Body005  label="caja-sensores"
  Group = -> [Sketch015,Pad011,Sketch016,Pad012,Sketch017,Pocket004,Sketch018,Pocket005,Sketch019,Pocket006,Sketch020,Pocket007,LinearPattern]
  Origin = -> Origin005
  Tip = -> LinearPattern
FEATURE [Sketcher::SketchObject] Sketch021
  MapMode = 5
  Support = -> [XY_Plane006]
  sketch-geometry (2):
    g0: Circle CenterX=25.5224 CenterY=95.7209 CenterZ=0 NormalX=0 NormalY=0 NormalZ=1 AngleXU=0 Radius=15
    g1: Circle CenterX=25.5224 CenterY=95.7209 CenterZ=0 NormalX=0 NormalY=0 NormalZ=1 AngleXU=0 Radius=20
  constraints (3):
    c: Coincident(g1,g0)
    c: Diameter(g1) = 40
    c: Diameter(g0) = 30
FEATURE [PartDesign::Pad] Pad013
  Length = 200
  Length2 = 100
  Profile = -> Sketch021
  Refine = true
  Type = 0
FEATURE [PartDesign::Plane] DatumPlane001
  AttachmentOffset = pos=(0,-29,0) rot=(1,0,0;1.5708rad)
  Length = 77.1185
  MapMode = 45
  Placement = pos=(25.5224,66.7209,100) rot=(1,0,0;1.5708rad)
  ResizeMode = 0
  Support = -> [Pad013]
  Width = 231.596
FEATURE [Sketcher::SketchObject] Sketch022
  MapMode = 5
  Placement = pos=(25.5224,66.7209,100) rot=(1,0,0;1.5708rad)
  Support = -> [DatumPlane001]
  sketch-geometry (2):
    g0: Circle CenterX=0 CenterY=-85 CenterZ=0 NormalX=0 NormalY=0 NormalZ=1 AngleXU=0 Radius=1.5
    g1: Circle CenterX=0 CenterY=85 CenterZ=0 NormalX=0 NormalY=0 NormalZ=1 AngleXU=0 Radius=1.5
  constraints (6):
    c: PointOnObject(g0,g-2)
    c: DistanceY(g0,g-1) = 85
    c: Diameter(g0) = 3
    c: PointOnObject(g1,g-2)
    c: Equal(g1,g0)
    c: DistanceY(g-1,g1) = 85
FEATURE [PartDesign::Pocket] Pocket008
  BaseFeature = -> Pad013
  Length = 5
  Length2 = 100
  Profile = -> Sketch022
  Refine = true
  Type = 1
FEATURE [PartDesign::Body] Body006  label="tubo-200mm"
  Group = -> [Sketch021,Pad013,DatumPlane001,Sketch022,Pocket008]
  Origin = -> Origin006
  Tip = -> Pocket008
FEATURE [Sketcher::SketchObject] Sketch023
  AttachmentOffset = pos=(200,100,0) rot=(0,0,1;0rad)
  MapMode = 5
  Placement = pos=(200,100,0) rot=(0,0,1;0rad)
  Support = -> [XY_Plane007]
  sketch-geometry (4):
    g0: LineSegment StartX=60 StartY=42.45 StartZ=0 EndX=120 EndY=42.45 EndZ=0
    g1: LineSegment StartX=120 StartY=42.45 StartZ=0 EndX=120 EndY=-42.45 EndZ=0
    g2: LineSegment StartX=120 StartY=-42.45 StartZ=0 EndX=60 EndY=-42.45 EndZ=0
    g3: LineSegment StartX=60 StartY=-42.45 StartZ=0 EndX=60 EndY=42.45 EndZ=0
  constraints (11):
    c: Coincident(g1,g2)
    c: Coincident(g2,g3)
    c: Coincident(g3,g0)
    c: Horizontal(g0)
    c: Horizontal(g2)
    c: DistanceY(g1,g1) = 84.9
    c: Symmetric(g2,g0,g-1)
    c: DistanceX(g-1,g2) = 60
    c: Coincident(g0,g1)
    c: DistanceX(g0,g0) = 60
    c: Equal(g2,g0)
FEATURE [PartDesign::Pad] Pad014
  Length = 2
  Length2 = 100
  Profile = -> Sketch023
  Refine = true
  Type = 0
FEATURE [Sketcher::SketchObject] Sketch024
  ExternalGeometry = -> [Pad014]
  MapMode = 5
  Placement = pos=(0,0,2) rot=(0,0,1;0rad)
  Support = -> [Pad014]
  sketch-geometry (4):
    g0: LineSegment StartX=261 StartY=141.45 StartZ=0 EndX=319 EndY=141.45 EndZ=0
    g1: LineSegment StartX=319 StartY=141.45 StartZ=0 EndX=319 EndY=58.55 EndZ=0
    g2: LineSegment StartX=319 StartY=58.55 StartZ=0 EndX=261 EndY=58.55 EndZ=0
    g3: LineSegment StartX=261 StartY=58.55 StartZ=0 EndX=261 EndY=141.45 EndZ=0
  constraints (12):
    c: Coincident(g0,g1)
    c: Coincident(g1,g2)
    c: Coincident(g2,g3)
    c: Coincident(g3,g0)
    c: Horizontal(g0)
    c: Horizontal(g2)
    c: Vertical(g1)
    c: Vertical(g3)
    c: DistanceX(g-3,g0) = 1
    c: DistanceY(g0,g-4) = 1
    c: DistanceX(g1,g-4) = 1
    c: DistanceY(g-4,g1) = 1
FEATURE [PartDesign::Pad] Pad015
  BaseFeature = -> Pad014
  Length = 3
  Length2 = 100
  Profile = -> Sketch024
  Refine = true
  Type = 0
FEATURE [Sketcher::SketchObject] Sketch025
  ExternalGeometry = -> [Pad015]
  MapMode = 5
  Placement = pos=(0,0,5) rot=(0,0,1;0rad)
  Support = -> [Pad015]
  sketch-geometry (27):
    g0: LineSegment StartX=261 StartY=141.45 StartZ=0 EndX=273 EndY=141.45 EndZ=0
    g1: LineSegment StartX=273 StartY=141.45 StartZ=0 EndX=273 EndY=139.45 EndZ=0
    g2: LineSegment StartX=273 StartY=139.45 StartZ=0 EndX=263 EndY=139.45 EndZ=0
    g3: LineSegment StartX=263 StartY=139.45 StartZ=0 EndX=263 EndY=129.45 EndZ=0
    g4: LineSegment StartX=263 StartY=129.45 StartZ=0 EndX=261 EndY=129.45 EndZ=0
    g5: LineSegment StartX=261 StartY=129.45 StartZ=0 EndX=261 EndY=141.45 EndZ=0
    g6: LineSegment StartX=319 StartY=141.45 StartZ=0 EndX=307 EndY=141.45 EndZ=0
    g7: LineSegment StartX=307 StartY=141.45 StartZ=0 EndX=307 EndY=139.45 EndZ=0
    g8: LineSegment StartX=307 StartY=139.45 StartZ=0 EndX=317 EndY=139.45 EndZ=0
    g9: LineSegment StartX=317 StartY=139.45 StartZ=0 EndX=317 EndY=129.45 EndZ=0
    g10: LineSegment StartX=317 StartY=129.45 StartZ=0 EndX=319 EndY=129.45 EndZ=0
    g11: LineSegment StartX=319 StartY=129.45 StartZ=0 EndX=319 EndY=141.45 EndZ=0
    g12: LineSegment [constr] StartX=319 StartY=141.45 StartZ=0 EndX=261 EndY=58.55 EndZ=0
    g13: LineSegment [constr] StartX=319 StartY=58.55 StartZ=0 EndX=290 EndY=100 EndZ=0
    g14: LineSegment [constr] StartX=271.067 StartY=100 StartZ=0 EndX=290 EndY=100 EndZ=0
    g15: LineSegment StartX=261 StartY=58.55 StartZ=0 EndX=273 EndY=58.55 EndZ=0
    g16: LineSegment StartX=273 StartY=58.55 StartZ=0 EndX=273 EndY=60.55 EndZ=0
    g17: LineSegment StartX=273 StartY=60.55 StartZ=0 EndX=263 EndY=60.55 EndZ=0
    g18: LineSegment StartX=263 StartY=60.55 StartZ=0 EndX=263 EndY=70.55 EndZ=0
    g19: LineSegment StartX=263 StartY=70.55 StartZ=0 EndX=261 EndY=70.55 EndZ=0
    g20: LineSegment StartX=261 StartY=70.55 StartZ=0 EndX=261 EndY=58.55 EndZ=0
    g21: LineSegment StartX=319 StartY=58.55 StartZ=0 EndX=307 EndY=58.55 EndZ=0
    g22: LineSegment StartX=307 StartY=58.55 StartZ=0 EndX=307 EndY=60.55 EndZ=0
    g23: LineSegment StartX=307 StartY=60.55 StartZ=0 EndX=317 EndY=60.55 EndZ=0
    g24: LineSegment StartX=317 StartY=60.55 StartZ=0 EndX=317 EndY=70.55 EndZ=0
    g25: LineSegment StartX=317 StartY=70.55 StartZ=0 EndX=319 EndY=70.55 EndZ=0
    g26: LineSegment StartX=319 StartY=70.55 StartZ=0 EndX=319 EndY=58.55 EndZ=0
  constraints (70):
    c: Coincident(g0,g1)
    c: Coincident(g1,g2)
    c: Horizontal(g0)
    c: Horizontal(g2)
    c: Vertical(g1)
    c: Coincident(g3,g4)
    c: Coincident(g4,g5)
    c: Horizontal(g4)
    c: Vertical(g3)
    c: Vertical(g5)
    c: Coincident(g6,g7)
    c: Coincident(g7,g8)
    c: Horizontal(g6)
    c: Horizontal(g8)
    c: Vertical(g7)
    c: Coincident(g9,g10)
    c: Coincident(g10,g11)
    c: Horizontal(g10)
    c: Vertical(g9)
    c: Vertical(g11)
    c: Coincident(g2,g3)
    c: Coincident(g9,g8)
    c: Equal(g1,g4)
    c: Equal(g4,g7)
    c: Equal(g7,g10)
    c: Coincident(g0,g5)
    c: Coincident(g0,g-4)
    c: Coincident(g-5,g11)
    c: Coincident(g6,g11)
    c: DistanceX(g10,g10) = 2
    c: Equal(g2,g3)
    c: Equal(g3,g8)
    c: Equal(g8,g9)
    c: DistanceX(g2,g2) = 10
    c: Coincident(g12,g6)
    c: Coincident(g12,g-6)
    c: Coincident(g13,g-6)
    c: PointOnObject(g13,g12)
    c: Horizontal(g14)
    c: Coincident(g14,g13)
    c: Coincident(g15,g16)
    c: Coincident(g16,g17)
    c: Horizontal(g15)
    c: Horizontal(g17)
    c: Vertical(g16)
    c: Coincident(g18,g19)
    c: Coincident(g19,g20)
    c: Horizontal(g19)
    c: Vertical(g18)
    c: Vertical(g20)
    c: Coincident(g21,g22)
    c: Coincident(g22,g23)
    c: Horizontal(g21)
    c: Horizontal(g23)
    c: Vertical(g22)
    c: Coincident(g24,g25)
    c: Coincident(g25,g26)
    c: Horizontal(g25)
    c: Vertical(g24)
    c: Vertical(g26)
    c: Coincident(g17,g18)
    c: Coincident(g24,g23)
    c: Equal(g16,g19)
    c: Equal(g19,g22)
    c: Equal(g22,g25)
    c: Coincident(g15,g20)
    c: Coincident(g21,g26)
    c: Equal(g17,g18)
    c: Equal(g18,g23)
    c: Equal(g23,g24)
FEATURE [PartDesign::Pad] Pad016
  BaseFeature = -> Pad015
  Length = 20
  Length2 = 100
  Profile = -> Sketch025
  Refine = true
  Type = 0
FEATURE [Sketcher::SketchObject] Sketch026
  ExternalGeometry = -> [Pad016]
  MapMode = 5
  Placement = pos=(0,0,5) rot=(0,0,1;0rad)
  Support = -> [Pad016]
  sketch-geometry (8):
    g0: LineSegment StartX=315 StartY=137.45 StartZ=0 EndX=264 EndY=137.45 EndZ=0
    g1: LineSegment StartX=266 StartY=135.45 StartZ=0 EndX=315 EndY=135.45 EndZ=0
    g2: LineSegment StartX=315 StartY=135.45 StartZ=0 EndX=315 EndY=137.45 EndZ=0
    g3: LineSegment StartX=266 StartY=135.45 StartZ=0 EndX=266 EndY=64.55 EndZ=0
    g4: LineSegment StartX=264 StartY=62.55 StartZ=0 EndX=264 EndY=137.45 EndZ=0
    g5: LineSegment StartX=264 StartY=62.55 StartZ=0 EndX=315 EndY=62.55 EndZ=0
    g6: LineSegment StartX=315 StartY=62.55 StartZ=0 EndX=315 EndY=64.55 EndZ=0
    g7: LineSegment StartX=315 StartY=64.55 StartZ=0 EndX=266 EndY=64.55 EndZ=0
  constraints (24):
    c: Coincident(g1,g2)
    c: Coincident(g2,g0)
    c: Horizontal(g0)
    c: Horizontal(g1)
    c: Vertical(g2)
    c: Vertical(g3)
    c: Vertical(g4)
    c: Coincident(g5,g6)
    c: Coincident(g6,g7)
    c: Horizontal(g5)
    c: Horizontal(g7)
    c: Vertical(g6)
    c: Coincident(g3,g1)
    c: Coincident(g7,g3)
    c: Equal(g2,g6)
    c: DistanceY(g2,g2) = 2
    c: Coincident(g0,g4)
    c: DistanceX(g4,g3) = 2
    c: Equal(g0,g5)
    c: Coincident(g5,g4)
    c: DistanceX(g-5,g4) = 3
    c: DistanceX(g6,g-6) = 4
    c: DistanceY(g-4,g5) = 4
    c: DistanceY(g0,g-3) = 4
FEATURE [Mesh::Feature] amplificador_2W  label="amplificador-2W"
  Placement = pos=(-5.5,69,351) rot=(-1,0,0;1.5708rad)
FEATURE [Sketcher::SketchObject] Sketch027
  MapMode = 5
  Placement = pos=(0,0,5) rot=(0,0,1;0rad)
  Support = -> [Pad016]
  sketch-geometry (22):
    g0: Circle CenterX=298.999 CenterY=96.3015 CenterZ=0 NormalX=0 NormalY=0 NormalZ=1 AngleXU=0 Radius=1.6
    g1: Circle CenterX=308.309 CenterY=91.9685 CenterZ=0 NormalX=0 NormalY=0 NormalZ=1 AngleXU=0 Radius=5
    g2: LineSegment StartX=300.386 StartY=124.023 StartZ=0 EndX=297.886 EndY=124.023 EndZ=0
    g3: LineSegment StartX=288.886 StartY=124.023 StartZ=0 EndX=288.886 EndY=102.755 EndZ=0
    g4: LineSegment StartX=288.886 StartY=102.755 StartZ=0 EndX=291.386 EndY=102.755 EndZ=0
    g5: LineSegment StartX=291.386 StartY=124.023 StartZ=0 EndX=291.386 EndY=102.755 EndZ=0
    g6: LineSegment StartX=293.386 StartY=124.023 StartZ=0 EndX=293.386 EndY=102.755 EndZ=0
    g7: LineSegment StartX=295.886 StartY=124.023 StartZ=0 EndX=295.886 EndY=102.755 EndZ=0
    g8: LineSegment StartX=297.886 StartY=124.023 StartZ=0 EndX=297.886 EndY=102.755 EndZ=0
    g9: LineSegment StartX=300.386 StartY=124.023 StartZ=0 EndX=300.386 EndY=102.755 EndZ=0
    g10: LineSegment StartX=302.386 StartY=124.283 StartZ=0 EndX=302.386 EndY=103.015 EndZ=0
    g11: LineSegment StartX=288.886 StartY=124.023 StartZ=0 EndX=291.386 EndY=124.023 EndZ=0
    g12: LineSegment StartX=295.886 StartY=124.023 StartZ=0 EndX=293.386 EndY=124.023 EndZ=0
    g13: LineSegment StartX=293.386 StartY=102.755 StartZ=0 EndX=295.886 EndY=102.755 EndZ=0
    g14: LineSegment StartX=297.886 StartY=102.755 StartZ=0 EndX=300.386 EndY=102.755 EndZ=0
    g15: LineSegment StartX=302.386 StartY=124.283 StartZ=0 EndX=304.886 EndY=124.283 EndZ=0
    g16: LineSegment StartX=304.886 StartY=124.283 StartZ=0 EndX=304.886 EndY=103.015 EndZ=0
    g17: LineSegment StartX=302.386 StartY=103.015 StartZ=0 EndX=304.886 EndY=103.015 EndZ=0
    g18: LineSegment StartX=306.886 StartY=124.298 StartZ=0 EndX=309.386 EndY=124.298 EndZ=0
    g19: LineSegment StartX=309.386 StartY=124.298 StartZ=0 EndX=309.386 EndY=103.03 EndZ=0
    g20: LineSegment StartX=309.386 StartY=103.03 StartZ=0 EndX=306.886 EndY=103.03 EndZ=0
    g21: LineSegment StartX=306.886 StartY=103.03 StartZ=0 EndX=306.886 EndY=124.298 EndZ=0
  constraints (57):
    c: Diameter(g0) = 3.2
    c: Diameter(g1) = 10
    c: Coincident(g3,g4)
    c: Horizontal(g4)
    c: Vertical(g5)
    c: Vertical(g6)
    c: Vertical(g7)
    c: Vertical(g8)
    c: Vertical(g3)
    c: Vertical(g9)
    c: Vertical(g10)
    c: Horizontal(g2)
    c: PointOnObject(g7,g4)
    c: Coincident(g11,g3)
    c: Coincident(g11,g5)
    c: Horizontal(g11)
    c: Coincident(g12,g6)
    c: Coincident(g2,g8)
    c: Coincident(g12,g7)
    c: Tangent(g2,g12)
    c: Coincident(g4,g5)
    c: Coincident(g13,g6)
    c: Tangent(g4,g13)
    c: PointOnObject(g13,g7)
    c: PointOnObject(g14,g8)
    c: Tangent(g13,g14)
    c: PointOnObject(g14,g9)
    c: Coincident(g2,g9)
    c: Equal(g11,g12)
    c: Equal(g12,g2)
    c: DistanceX(g11,g11) = 2.5
    c: DistanceX(g5,g6) = 2
    c: DistanceX(g7,g2) = 2
    c: Coincident(g10,g15)
    c: Coincident(g15,g16)
    c: Vertical(g16)
    c: Equal(g3,g6)
    c: Equal(g6,g8)
    c: Equal(g8,g9)
    c: Equal(g9,g10)
    c: Equal(g10,g16)
    c: Horizontal(g17)
    c: Coincident(g17,g10)
    c: Coincident(g16,g17)
    c: Equal(g2,g15)
    c: DistanceX(g2,g10) = 2
    c: Coincident(g18,g19)
    c: Coincident(g19,g20)
    c: Coincident(g20,g21)
    c: Coincident(g21,g18)
    c: Horizontal(g18)
    c: Horizontal(g20)
    c: Vertical(g19)
    c: Vertical(g21)
    c: Equal(g18,g15)
    c: Equal(g21,g16)
    c: DistanceX(g15,g18) = 2
FEATURE [PartDesign::Pocket] Pocket009
  BaseFeature = -> Pad016
  Length = 5
  Length2 = 100
  Profile = -> Sketch027
  Refine = true
  Type = 0
FEATURE [PartDesign::Pad] Pad017
  BaseFeature = -> Pocket009
  Length = 70
  Length2 = 100
  Profile = -> Sketch026
  Refine = true
  Type = 0
FEATURE [Sketcher::SketchObject] Sketch030
  MapMode = 5
  Support = -> [XY_Plane008]
  sketch-geometry (4):
    g0: LineSegment StartX=-166.57 StartY=50 StartZ=0 EndX=-66.5705 EndY=50 EndZ=0
    g1: LineSegment StartX=-66.5705 StartY=50 StartZ=0 EndX=-66.5705 EndY=-50 EndZ=0
    g2: LineSegment StartX=-66.5705 StartY=-50 StartZ=0 EndX=-166.57 EndY=-50 EndZ=0
    g3: LineSegment StartX=-166.57 StartY=-50 StartZ=0 EndX=-166.57 EndY=50 EndZ=0
  constraints (10):
    c: Coincident(g0,g1)
    c: Coincident(g1,g2)
    c: Coincident(g2,g3)
    c: Coincident(g3,g0)
    c: Horizontal(g0)
    c: Horizontal(g2)
    c: Vertical(g3)
    c: Symmetric(g1,g0,g-1)
    c: Equal(g0,g1)
    c: DistanceX(g0,g0) = 100
FEATURE [PartDesign::Pad] Pad018
  Length = 3
  Length2 = 100
  Profile = -> Sketch030
  Refine = true
  Type = 0
FEATURE [Sketcher::SketchObject] Sketch031
  ExternalGeometry = -> [Pad018]
  MapMode = 5
  Placement = pos=(0,0,3) rot=(0,0,1;0rad)
  Support = -> [Pad018]
  sketch-geometry (12):
    g0: LineSegment StartX=-166.57 StartY=50 StartZ=0 EndX=-66.5705 EndY=50 EndZ=0
    g1: LineSegment StartX=-66.5705 StartY=50 StartZ=0 EndX=-66.5705 EndY=-50 EndZ=0
    g2: LineSegment StartX=-66.5705 StartY=-50 StartZ=0 EndX=-166.57 EndY=-50 EndZ=0
    g3: LineSegment StartX=-166.57 StartY=-50 StartZ=0 EndX=-166.57 EndY=50 EndZ=0
    g4: LineSegment StartX=-163.57 StartY=47 StartZ=0 EndX=-107.57 EndY=47 EndZ=0
    g5: LineSegment StartX=-69.5705 StartY=47 StartZ=0 EndX=-69.5705 EndY=-47 EndZ=0
    g6: LineSegment StartX=-69.5705 StartY=-47 StartZ=0 EndX=-104.57 EndY=-47 EndZ=0
    g7: LineSegment StartX=-163.57 StartY=-47 StartZ=0 EndX=-163.57 EndY=47 EndZ=0
    g8: LineSegment StartX=-104.57 StartY=47 StartZ=0 EndX=-104.57 EndY=-47 EndZ=0
    g9: LineSegment StartX=-107.57 StartY=-47 StartZ=0 EndX=-107.57 EndY=47 EndZ=0
    g10: LineSegment StartX=-104.57 StartY=47 StartZ=0 EndX=-69.5705 EndY=47 EndZ=0
    g11: LineSegment StartX=-107.57 StartY=-47 StartZ=0 EndX=-163.57 EndY=-47 EndZ=0
  constraints (32):
    c: Coincident(g0,g1)
    c: Coincident(g1,g2)
    c: Coincident(g2,g3)
    c: Coincident(g3,g0)
    c: Horizontal(g0)
    c: Horizontal(g2)
    c: Vertical(g1)
    c: Vertical(g3)
    c: Coincident(g0,g-3)
    c: Coincident(g1,g-4)
    c: Coincident(g10,g5)
    c: Coincident(g5,g6)
    c: Coincident(g11,g7)
    c: Coincident(g7,g4)
    c: Horizontal(g4)
    c: Horizontal(g6)
    c: Vertical(g5)
    c: Vertical(g7)
    c: DistanceX(g10,g0) = 3
    c: DistanceX(g0,g4) = 3
    c: DistanceY(g10,g0) = 3
    c: DistanceY(g1,g5) = 3
    c: Vertical(g8)
    c: Vertical(g9)
    c: DistanceX(g8,g10) = 35
    c: Tangent(g4,g10)
    c: Coincident(g6,g8)
    c: Tangent(g6,g11)
    c: DistanceX(g9,g6) = 3
    c: Coincident(g4,g9)
    c: Coincident(g8,g10)
    c: Coincident(g11,g9)
FEATURE [PartDesign::Pad] Pad019
  BaseFeature = -> Pad018
  Length = 97
  Length2 = 100
  Profile = -> Sketch031
  Refine = true
  Type = 0
FEATURE [Sketcher::SketchObject] Sketch032
  ExternalGeometry = -> [Pad019]
  MapMode = 5
  Placement = pos=(-166.57,0,0) rot=(0.57735,-0.57735,-0.57735;2.0944rad)
  Support = -> [Pad019]
  sketch-geometry (13):
    g0: LineSegment StartX=-45 StartY=3 StartZ=0 EndX=-9.99999 EndY=3 EndZ=0
    g1: LineSegment [constr] StartX=17.4932 StartY=64.8878 StartZ=0 EndX=3.6e-15 EndY=64.8878 EndZ=0
    g2: ArcOfCircle CenterX=9 CenterY=12 CenterZ=0 NormalX=0 NormalY=0 NormalZ=1 AngleXU=0 Radius=54.7449 StartAngle=1.92792 EndAngle=3.30674
    g3: ArcOfCircle CenterX=-9 CenterY=12 CenterZ=0 NormalX=0 NormalY=0 NormalZ=1 AngleXU=0 Radius=54.7449 StartAngle=6.11804 EndAngle=7.49685
    g4: ArcOfCircle CenterX=1.8e-15 CenterY=36.1205 CenterZ=0 NormalX=0 NormalY=0 NormalZ=1 AngleXU=0 Radius=29 StartAngle=1.21367 EndAngle=1.92792
    g5: LineSegment [constr] StartX=-9 StartY=12 StartZ=0 EndX=9 EndY=12 EndZ=0
    g6: Circle CenterX=2e-16 CenterY=10 CenterZ=0 NormalX=0 NormalY=0 NormalZ=1 AngleXU=0 Radius=1.6
    g7: ArcOfCircle CenterX=2e-16 CenterY=10 CenterZ=0 NormalX=0 NormalY=0 NormalZ=1 AngleXU=0 Radius=5 StartAngle=0.510929 EndAngle=2.63066
    g8: LineSegment StartX=-4.36145 StartY=12.4449 StartZ=0 EndX=-9.99999 EndY=3 EndZ=0
    g9: LineSegment StartX=4.36145 StartY=12.4449 StartZ=0 EndX=9.99999 EndY=3 EndZ=0
    g10: LineSegment StartX=9.99999 StartY=3 StartZ=0 EndX=45 EndY=3 EndZ=0
    g11: Circle CenterX=-35 CenterY=85 CenterZ=0 NormalX=0 NormalY=0 NormalZ=1 AngleXU=0 Radius=1.6
    g12: Circle CenterX=35 CenterY=85 CenterZ=0 NormalX=0 NormalY=0 NormalZ=1 AngleXU=0 Radius=1.6
  constraints (31):
    c: Horizontal(g0)
    c: DistanceY(g-3,g10) = 3
    c: DistanceX(g10,g-3) = 5
    c: Horizontal(g1)
    c: Coincident(g2,g0)
    c: DistanceX(g-3,g0) = 5
    c: PointOnObject(g1,g-2)
    c: Tangent(g2,g4) = -1.5708
    c: Tangent(g3,g4) = -1.5708
    c: Symmetric(g2,g3,g-2)
    c: Coincident(g10,g3)
    c: Coincident(g5,g3)
    c: Coincident(g5,g2)
    c: DistanceX(g3,g-1) = 9
    c: DistanceY(g-1,g2) = 12
    c: Symmetric(g2,g3,g-2)
    c: Radius(g4) = 29
    c: Diameter(g6) = 3.2
    c: Coincident(g7,g6)
    c: Diameter(g7) = 10
    c: DistanceY(g-1,g6) = 10
    c: Coincident(g0,g8)
    c: Tangent(g0,g10)
    c: Coincident(g7,g8)
    c: Coincident(g9,g10)
    c: Coincident(g9,g7)
    c: Symmetric(g7,g7,g-2)
    c: Equal(g8,g9)
    c: Distance(g8) = 11
    c: DistanceX(g-4,g11) = 15
    c: DistanceY(g11,g-4) = 15
FEATURE [PartDesign::Pocket] Pocket012
  BaseFeature = -> Pad019
  Length = 10
  Length2 = 100
  Profile = -> Sketch032
  Refine = true
  Type = 0
FEATURE [Mesh::Feature] Arduino
  Placement = pos=(19,66,76) rot=(0,0,1;1.5708rad)
FEATURE [Mesh::Feature] hub
  Placement = pos=(-112,86,79) rot=(0.57735,-0.57735,-0.57735;2.0944rad)
FEATURE [Sketcher::SketchObject] Sketch033
  MapMode = 5
  Placement = pos=(-107.57,0,0) rot=(0.57735,-0.57735,-0.57735;2.0944rad)
  Support = -> [Pocket012]
  sketch-geometry (8):
    g0: Circle CenterX=-28.8265 CenterY=95.2682 CenterZ=0 NormalX=0 NormalY=0 NormalZ=1 AngleXU=0 Radius=1.6
    g1: Circle CenterX=13.2949 CenterY=95.2639 CenterZ=0 NormalX=0 NormalY=0 NormalZ=1 AngleXU=0 Radius=1.6
    g2: Circle CenterX=-28.7795 CenterY=62.6953 CenterZ=0 NormalX=0 NormalY=0 NormalZ=1 AngleXU=0 Radius=1.6
    g3: Circle CenterX=13.2933 CenterY=62.7239 CenterZ=0 NormalX=0 NormalY=0 NormalZ=1 AngleXU=0 Radius=1.6
    g4: Circle CenterX=-21.8922 CenterY=50.1389 CenterZ=0 NormalX=0 NormalY=0 NormalZ=1 AngleXU=0 Radius=1.6
    g5: Circle CenterX=30.2332 CenterY=55.2089 CenterZ=0 NormalX=0 NormalY=0 NormalZ=1 AngleXU=0 Radius=1.6
    g6: Circle CenterX=-21.8638 CenterY=22.1894 CenterZ=0 NormalX=0 NormalY=0 NormalZ=1 AngleXU=0 Radius=1.6
    g7: Circle CenterX=28.9089 CenterY=6.93878 CenterZ=0 NormalX=0 NormalY=0 NormalZ=1 AngleXU=0 Radius=1.6
  constraints (8):
    c: Equal(g0,g1)
    c: Equal(g1,g2)
    c: Equal(g2,g3)
    c: Equal(g3,g4)
    c: Equal(g4,g5)
    c: Equal(g5,g6)
    c: Equal(g6,g7)
    c: Diameter(g1) = 3.2
FEATURE [PartDesign::Pocket] Pocket013
  BaseFeature = -> Pocket012
  Length = 5
  Length2 = 100
  Profile = -> Sketch033
  Refine = true
  Type = 0
FEATURE [Sketcher::SketchObject] Sketch034
  MapMode = 5
  Placement = pos=(0,-50,0) rot=(1,0,0;1.5708rad)
  Support = -> [Pocket013]
  sketch-geometry (9):
    g0: LineSegment StartX=-111 StartY=59 StartZ=0 EndX=-111 EndY=3 EndZ=0
    g1: LineSegment StartX=-111 StartY=3 StartZ=0 EndX=-124 EndY=3 EndZ=0
    g2: LineSegment StartX=-124 StartY=3 StartZ=0 EndX=-124 EndY=24.0071 EndZ=0
    g3: LineSegment StartX=-124 StartY=59 StartZ=0 EndX=-111 EndY=59 EndZ=0
    g4: LineSegment StartX=-127 StartY=29.4001 StartZ=0 EndX=-127 EndY=37.4001 EndZ=0
    g5: LineSegment StartX=-124 StartY=42.7932 StartZ=0 EndX=-124 EndY=59 EndZ=0
    g6: LineSegment StartX=-127 StartY=29.4001 StartZ=0 EndX=-124 EndY=24.0071 EndZ=0
    g7: LineSegment [constr] StartX=-129.962 StartY=33.4001 StartZ=0 EndX=-123.904 EndY=33.4001 EndZ=0
    g8: LineSegment StartX=-127 StartY=37.4001 StartZ=0 EndX=-124 EndY=42.7932 EndZ=0
  constraints (22):
    c: Coincident(g0,g1)
    c: Coincident(g1,g2)
    c: Horizontal(g1)
    c: Vertical(g0)
    c: Vertical(g2)
    c: Horizontal(g3)
    c: DistanceX(g1,g-1) = 124
    c: DistanceX(g1,g1) = 13
    c: Coincident(g5,g3)
    c: Coincident(g0,g3)
    c: DistanceY(g0,g0) = 56
    c: DistanceY(g-1,g0) = 3
    c: Vertical(g4)
    c: Tangent(g2,g5)
    c: DistanceY(g4,g4) = 8
    c: Coincident(g2,g6)
    c: Horizontal(g7)
    c: DistanceY(g7,g4) = 4
    c: Coincident(g4,g8)
    c: Coincident(g4,g6)
    c: Coincident(g5,g8)
    c: DistanceX(g4,g5) = 3
FEATURE [PartDesign::Pocket] Pocket014
  BaseFeature = -> Pocket013
  Length = 5
  Length2 = 100
  Profile = -> Sketch034
  Refine = true
  Type = 0
FEATURE [Sketcher::SketchObject] Sketch035
  MapMode = 5
  Support = -> [XY_Plane009]
  sketch-geometry (4):
    g0: LineSegment StartX=-166.957 StartY=162.893 StartZ=0 EndX=-66.9567 EndY=162.893 EndZ=0
    g1: LineSegment StartX=-66.9567 StartY=162.893 StartZ=0 EndX=-66.9567 EndY=62.8932 EndZ=0
    g2: LineSegment StartX=-66.9567 StartY=62.8932 StartZ=0 EndX=-166.957 EndY=62.8932 EndZ=0
    g3: LineSegment StartX=-166.957 StartY=62.8932 StartZ=0 EndX=-166.957 EndY=162.893 EndZ=0
  constraints (10):
    c: Coincident(g0,g1)
    c: Coincident(g1,g2)
    c: Coincident(g2,g3)
    c: Coincident(g3,g0)
    c: Horizontal(g0)
    c: Horizontal(g2)
    c: Vertical(g1)
    c: Vertical(g3)
    c: Equal(g3,g0)
    c: DistanceY(g1,g1) = 100
FEATURE [PartDesign::Pad] Pad020
  Length = 1
  Length2 = 100
  Profile = -> Sketch035
  Refine = true
  Type = 0
FEATURE [Sketcher::SketchObject] Sketch036
  ExternalGeometry = -> [Pad020]
  MapMode = 5
  Placement = pos=(0,0,1) rot=(0,0,1;0rad)
  Support = -> [Pad020]
  sketch-geometry (4):
    g0: LineSegment StartX=-163.957 StartY=159.893 StartZ=0 EndX=-69.9567 EndY=159.893 EndZ=0
    g1: LineSegment StartX=-69.9567 StartY=159.893 StartZ=0 EndX=-69.9567 EndY=65.8932 EndZ=0
    g2: LineSegment StartX=-69.9567 StartY=65.8932 StartZ=0 EndX=-163.957 EndY=65.8932 EndZ=0
    g3: LineSegment StartX=-163.957 StartY=65.8932 StartZ=0 EndX=-163.957 EndY=159.893 EndZ=0
  constraints (12):
    c: Coincident(g0,g1)
    c: Coincident(g1,g2)
    c: Coincident(g2,g3)
    c: Coincident(g3,g0)
    c: Horizontal(g0)
    c: Horizontal(g2)
    c: Vertical(g1)
    c: Vertical(g3)
    c: DistanceY(g-5,g1) = 3
    c: DistanceX(g0,g-5) = 3
    c: DistanceX(g-4,g0) = 3
    c: DistanceY(g0,g-4) = 3
FEATURE [PartDesign::Pad] Pad021
  BaseFeature = -> Pad020
  Length = 5
  Length2 = 100
  Profile = -> Sketch036
  Refine = true
  Type = 0
FEATURE [Sketcher::SketchObject] Sketch037
  ExternalGeometry = -> [Pad021]
  MapMode = 5
  Placement = pos=(0,0,6) rot=(0,0,1;0rad)
  Support = -> [Pad021]
  sketch-geometry (27):
    g0: LineSegment StartX=-163.957 StartY=159.893 StartZ=0 EndX=-153.957 EndY=159.893 EndZ=0
    g1: LineSegment StartX=-153.957 StartY=159.893 StartZ=0 EndX=-153.957 EndY=157.893 EndZ=0
    g2: LineSegment StartX=-153.957 StartY=157.893 StartZ=0 EndX=-161.957 EndY=157.893 EndZ=0
    g3: LineSegment StartX=-161.957 StartY=157.893 StartZ=0 EndX=-161.957 EndY=149.893 EndZ=0
    g4: LineSegment StartX=-161.957 StartY=149.893 StartZ=0 EndX=-163.957 EndY=149.893 EndZ=0
    g5: LineSegment StartX=-163.957 StartY=149.893 StartZ=0 EndX=-163.957 EndY=159.893 EndZ=0
    g6: LineSegment StartX=-69.9567 StartY=159.893 StartZ=0 EndX=-79.9567 EndY=159.893 EndZ=0
    g7: LineSegment StartX=-79.9567 StartY=159.893 StartZ=0 EndX=-79.9567 EndY=157.893 EndZ=0
    g8: LineSegment StartX=-79.9567 StartY=157.893 StartZ=0 EndX=-71.9567 EndY=157.893 EndZ=0
    g9: LineSegment StartX=-71.9567 StartY=157.893 StartZ=0 EndX=-71.9567 EndY=149.893 EndZ=0
    g10: LineSegment StartX=-71.9567 StartY=149.893 StartZ=0 EndX=-69.9567 EndY=149.893 EndZ=0
    g11: LineSegment StartX=-69.9567 StartY=149.893 StartZ=0 EndX=-69.9567 EndY=159.893 EndZ=0
    g12: LineSegment [constr] StartX=-163.957 StartY=65.8932 StartZ=0 EndX=-69.9567 EndY=159.893 EndZ=0
    g13: LineSegment [constr] StartX=-69.9567 StartY=65.8932 StartZ=0 EndX=-116.957 EndY=112.893 EndZ=0
    g14: LineSegment [constr] StartX=-156.164 StartY=112.893 StartZ=0 EndX=-81.1894 EndY=112.893 EndZ=0
    g15: LineSegment StartX=-163.957 StartY=65.8932 StartZ=0 EndX=-153.957 EndY=65.8932 EndZ=0
    g16: LineSegment StartX=-153.957 StartY=65.8932 StartZ=0 EndX=-153.957 EndY=67.9481 EndZ=0
    g17: LineSegment StartX=-153.957 StartY=67.9481 StartZ=0 EndX=-161.902 EndY=67.9481 EndZ=0
    g18: LineSegment StartX=-161.902 StartY=67.9481 StartZ=0 EndX=-161.902 EndY=75.8932 EndZ=0
    g19: LineSegment StartX=-161.902 StartY=75.8932 StartZ=0 EndX=-163.957 EndY=75.8932 EndZ=0
    g20: LineSegment StartX=-163.957 StartY=75.8932 StartZ=0 EndX=-163.957 EndY=65.8932 EndZ=0
    g21: LineSegment StartX=-69.9567 StartY=65.8932 StartZ=0 EndX=-79.9567 EndY=65.8932 EndZ=0
    g22: LineSegment StartX=-79.9567 StartY=65.8932 StartZ=0 EndX=-79.9567 EndY=67.9481 EndZ=0
    g23: LineSegment StartX=-79.9567 StartY=67.9481 StartZ=0 EndX=-72.0116 EndY=67.9481 EndZ=0
    g24: LineSegment StartX=-72.0116 StartY=67.9481 StartZ=0 EndX=-72.0116 EndY=75.8932 EndZ=0
    g25: LineSegment StartX=-72.0116 StartY=75.8932 StartZ=0 EndX=-69.9567 EndY=75.8932 EndZ=0
    g26: LineSegment StartX=-69.9567 StartY=75.8932 StartZ=0 EndX=-69.9567 EndY=65.8932 EndZ=0
  constraints (74):
    c: Coincident(g0,g1)
    c: Coincident(g1,g2)
    c: Horizontal(g0)
    c: Horizontal(g2)
    c: Vertical(g1)
    c: Coincident(g3,g4)
    c: Coincident(g4,g5)
    c: Horizontal(g4)
    c: Vertical(g3)
    c: Vertical(g5)
    c: Coincident(g6,g7)
    c: Coincident(g7,g8)
    c: Horizontal(g6)
    c: Horizontal(g8)
    c: Vertical(g7)
    c: Coincident(g9,g10)
    c: Coincident(g10,g11)
    c: Horizontal(g10)
    c: Vertical(g9)
    c: Vertical(g11)
    c: Coincident(g3,g2)
    c: Coincident(g9,g8)
    c: Equal(g6,g11)
    c: Equal(g11,g0)
    c: Equal(g0,g5)
    c: Coincident(g0,g-4)
    c: Coincident(g0,g5)
    c: Coincident(g11,g-5)
    c: Coincident(g11,g6)
    c: DistanceY(g5,g5) = 10
    c: Equal(g4,g1)
    c: Equal(g1,g7)
    c: Equal(g7,g10)
    c: DistanceY(g1,g1) = 2
    c: Coincident(g12,g-6)
    c: Coincident(g12,g6)
    c: Coincident(g13,g-6)
    c: PointOnObject(g13,g12)
    c: Perpendicular(g12,g13)
    c: Horizontal(g14)
    c: PointOnObject(g13,g14)
    c: Coincident(g15,g16)
    c: Coincident(g16,g17)
    c: Horizontal(g15)
    c: Horizontal(g17)
    c: Vertical(g16)
    c: Coincident(g18,g19)
    c: Coincident(g19,g20)
    c: Horizontal(g19)
    c: Vertical(g18)
    c: Vertical(g20)
    c: Coincident(g21,g22)
    c: Coincident(g22,g23)
    c: Horizontal(g21)
    c: Horizontal(g23)
    c: Vertical(g22)
    c: Coincident(g24,g25)
    c: Coincident(g25,g26)
    c: Horizontal(g25)
    c: Vertical(g24)
    c: Vertical(g26)
    c: Coincident(g18,g17)
    c: Coincident(g24,g23)
    c: Equal(g21,g26)
    c: Equal(g26,g15)
    c: Equal(g15,g20)
    c: Coincident(g15,g20)
    c: Coincident(g26,g21)
    c: Equal(g19,g16)
    c: Equal(g16,g22)
    c: Equal(g22,g25)
    c: DistanceY(g26,g26) = 10
    c: Coincident(g21,g13)
    c: Coincident(g12,g15)
FEATURE [PartDesign::Pad] Pad022
  BaseFeature = -> Pad021
  Length = 20
  Length2 = 100
  Profile = -> Sketch037
  Refine = true
  Type = 0
FEATURE [PartDesign::Chamfer] Chamfer001
  Base = -> Pad022 [Edge2,Edge3,Edge18,Edge17,Edge13,Edge12,Edge7,Edge8]
  BaseFeature = -> Pad022
  Size = 2
FEATURE [Sketcher::SketchObject] Sketch038
  ExternalGeometry = -> [Chamfer001]
  MapMode = 5
  Placement = pos=(0,0,6) rot=(0,0,1;0rad)
  Support = -> [Chamfer001]
  sketch-geometry (13):
    g0: LineSegment StartX=-109.957 StartY=160.896 StartZ=0 EndX=-99.9567 EndY=160.896 EndZ=0
    g1: LineSegment StartX=-99.9567 StartY=160.896 StartZ=0 EndX=-99.9567 EndY=150.889 EndZ=0
    g2: LineSegment StartX=-99.9567 StartY=64.4762 StartZ=0 EndX=-109.957 EndY=64.4762 EndZ=0
    g3: LineSegment StartX=-109.957 StartY=64.4762 StartZ=0 EndX=-109.957 EndY=74.4762 EndZ=0
    g4: LineSegment StartX=-119.957 StartY=150.896 StartZ=0 EndX=-109.957 EndY=150.896 EndZ=0
    g5: LineSegment StartX=-109.957 StartY=74.4762 StartZ=0 EndX=-119.957 EndY=74.4762 EndZ=0
    g6: LineSegment StartX=-119.957 StartY=74.4762 StartZ=0 EndX=-119.957 EndY=150.896 EndZ=0
    g7: LineSegment StartX=-109.957 StartY=150.896 StartZ=0 EndX=-109.957 EndY=160.896 EndZ=0
    g8: LineSegment StartX=-89.9567 StartY=160.889 StartZ=0 EndX=-99.9567 EndY=160.889 EndZ=0
    g9: LineSegment StartX=-89.9567 StartY=150.889 StartZ=0 EndX=-99.9567 EndY=150.889 EndZ=0
    g10: LineSegment StartX=-89.9567 StartY=74.476 StartZ=0 EndX=-89.9567 EndY=150.889 EndZ=0
    g11: LineSegment StartX=-99.9567 StartY=74.476 StartZ=0 EndX=-89.9567 EndY=74.476 EndZ=0
    g12: LineSegment StartX=-99.9567 StartY=74.476 StartZ=0 EndX=-99.9567 EndY=64.4762 EndZ=0
  constraints (31):
    c: Coincident(g0,g1)
    c: Coincident(g12,g2)
    c: Coincident(g2,g3)
    c: Coincident(g7,g0)
    c: Horizontal(g0)
    c: Horizontal(g2)
    c: Vertical(g1)
    c: Vertical(g3)
    c: DistanceX(g12,g-3) = 30
    c: DistanceX(g0,g0) = 10
    c: Coincident(g5,g6)
    c: Coincident(g6,g4)
    c: Horizontal(g4)
    c: Horizontal(g5)
    c: Vertical(g6)
    c: Tangent(g3,g7)
    c: Coincident(g4,g7)
    c: Coincident(g5,g3)
    c: Equal(g3,g7)
    c: DistanceY(g7,g7) = 10
    c: DistanceX(g4,g4) = 10
    c: Horizontal(g8)
    c: Coincident(g11,g10)
    c: Coincident(g10,g9)
    c: Horizontal(g9)
    c: Horizontal(g11)
    c: Vertical(g10)
    c: Equal(g9,g4)
    c: Coincident(g1,g9)
    c: Coincident(g12,g11)
    c: Tangent(g1,g12)
FEATURE [PartDesign::Pocket] Pocket015
  BaseFeature = -> Chamfer001
  Length = 5
  Length2 = 100
  Profile = -> Sketch038
  Refine = true
  Type = 0
FEATURE [PartDesign::Body] Body009  label="tapa-posterior-base"
  Group = -> [Sketch035,Pad020,Sketch036,Pad021,Sketch037,Pad022,Chamfer001,Sketch038,Pocket015]
  Origin = -> Origin009
  Tip = -> Pocket015
FEATURE [Sketcher::SketchObject] Sketch039
  MapMode = 5
  Support = -> [XY_Plane010]
  sketch-geometry (5):
    g0: LineSegment StartX=50.384 StartY=163.554 StartZ=0 EndX=150.384 EndY=163.554 EndZ=0
    g1: LineSegment StartX=150.384 StartY=163.554 StartZ=0 EndX=150.384 EndY=263.554 EndZ=0
    g2: LineSegment StartX=150.384 StartY=263.554 StartZ=0 EndX=50.384 EndY=263.554 EndZ=0
    g3: LineSegment StartX=50.384 StartY=263.554 StartZ=0 EndX=50.384 EndY=163.554 EndZ=0
    g4: Circle CenterX=100.384 CenterY=209.304 CenterZ=0 NormalX=0 NormalY=0 NormalZ=1 AngleXU=0 Radius=12
  constraints (13):
    c: Coincident(g0,g1)
    c: Coincident(g1,g2)
    c: Coincident(g2,g3)
    c: Coincident(g3,g0)
    c: Horizontal(g0)
    c: Horizontal(g2)
    c: Vertical(g1)
    c: Vertical(g3)
    c: Equal(g0,g3)
    c: DistanceX(g2,g2) = 100
    c: DistanceX(g4,g1) = 50
    c: DistanceY(g4,g1) = 54.25
    c: Radius(g4) = 12
FEATURE [PartDesign::Pad] Pad023
  Length = 5
  Length2 = 100
  Profile = -> Sketch039
  Refine = true
  Type = 0
FEATURE [Sketcher::SketchObject] Sketch040
  ExternalGeometry = -> [Pad023]
  MapMode = 5
  Placement = pos=(0,0,5) rot=(0,0,1;0rad)
  Support = -> [Pad023]
  sketch-geometry (2):
    g0: Circle CenterX=100.384 CenterY=209.304 CenterZ=0 NormalX=0 NormalY=0 NormalZ=1 AngleXU=0 Radius=25
    g1: Circle CenterX=100.384 CenterY=209.304 CenterZ=0 NormalX=0 NormalY=0 NormalZ=1 AngleXU=0 Radius=20.25
  constraints (4):
    c: Coincident(g0,g-3)
    c: Coincident(g1,g0)
    c: Diameter(g1) = 40.5
    c: Diameter(g0) = 50
FEATURE [PartDesign::Pad] Pad024
  BaseFeature = -> Pad023
  Length = 30
  Length2 = 100
  Profile = -> Sketch040
  Refine = true
  Type = 0
FEATURE [PartDesign::Plane] DatumPlane002
  AttachmentOffset = pos=(-35,0,0) rot=(0,1,0;1.5708rad)
  Length = 67.19
  MapMode = 45
  Placement = pos=(65.384,209.304,20) rot=(0,1,0;1.5708rad)
  ResizeMode = 0
  Support = -> [Pad024]
  Width = 295.744
FEATURE [Sketcher::SketchObject] Sketch041
  MapMode = 5
  Placement = pos=(65.384,209.304,20) rot=(0,1,0;1.5708rad)
  Support = -> [DatumPlane002]
  sketch-geometry (1):
    g0: Circle CenterX=0 CenterY=0 CenterZ=0 NormalX=0 NormalY=0 NormalZ=1 AngleXU=0 Radius=1.6
  constraints (2):
    c: Diameter(g0) = 3.2
    c: Coincident(g0,g-1)
FEATURE [PartDesign::Pocket] Pocket016
  BaseFeature = -> Pad024
  Length = 5
  Length2 = 100
  Profile = -> Sketch041
  Refine = true
  Reversed = true
  Type = 1
FEATURE [Part::FeaturePython] Clone  label="tapa-posterior-verde-e"  # Draft clone (typed FeaturePython)
  AttacherType = Attacher::AttachEngine3D
  Fuse = false
  Objects = -> [Chamfer]
  Placement = pos=(-50,45.5,415) rot=(0.707107,0,0.707107;3.14159rad)
  Scale = (1,1,1)
FEATURE [Part::FeaturePython] Clone006  label="tubo-200mm-e"  # Draft clone (typed FeaturePython)
  AttacherType = Attacher::AttachEngine3D
  Fuse = false
  Objects = -> [Pocket008]
  Placement = pos=(-26,-50,106) rot=(0,0,1;0rad)
  Scale = (1,1,1)
FEATURE [Part::FeaturePython] Clone012  label="tapa-posterior-amarillo-e"  # Draft clone (typed FeaturePython)
  AttacherType = Attacher::AttachEngine3D
  Fuse = false
  Objects = -> [Chamfer]
  Placement = pos=(-50,45.5,500) rot=(0.707107,0,0.707107;3.14159rad)
  Scale = (1,1,1)
FEATURE [Part::FeaturePython] Clone013  label="tapa-posterior-rojo-e"  # Draft clone (typed FeaturePython)
  AttacherType = Attacher::AttachEngine3D
  Fuse = false
  Objects = -> [Chamfer]
  Placement = pos=(-50,45.5,585) rot=(0.707107,0,0.707107;3.14159rad)
  Scale = (1,1,1)
FEATURE [Sketcher::SketchObject] Sketch042
  ExternalGeometry = -> [Pad017]
  MapMode = 5
  Placement = pos=(266,0,0) rot=(0.57735,0.57735,0.57735;2.0944rad)
  Support = -> [Pad017]
  sketch-geometry (4):
    g0: LineSegment StartX=84.55 StartY=80 StartZ=0 EndX=114.55 EndY=80 EndZ=0
    g1: LineSegment StartX=114.55 StartY=80 StartZ=0 EndX=114.55 EndY=40 EndZ=0
    g2: LineSegment StartX=84.55 StartY=40 StartZ=0 EndX=84.55 EndY=80 EndZ=0
    g3: ArcOfCircle CenterX=99.55 CenterY=41.0353 CenterZ=0 NormalX=0 NormalY=0 NormalZ=1 AngleXU=0 Radius=15.0357 StartAngle=3.2105 EndAngle=6.21427
  constraints (10):
    c: Coincident(g0,g1)
    c: Coincident(g2,g0)
    c: Horizontal(g0)
    c: Vertical(g1)
    c: Vertical(g2)
    c: DistanceX(g2,g1) = 30
    c: DistanceX(g-3,g0) = 20
    c: DistanceY(g-4,g0) = 5
    c: DistanceY(g1,g1) = 40
    c: Coincident(g3,g1)
FEATURE [PartDesign::Pocket] Pocket017
  BaseFeature = -> Pad017
  Length = 5
  Length2 = 100
  Profile = -> Sketch042
  Refine = true
  Type = 0
FEATURE [Sketcher::SketchObject] Sketch043
  ExternalGeometry = -> [Pocket017]
  MapMode = 5
  Placement = pos=(266,0,0) rot=(0.57735,0.57735,0.57735;2.0944rad)
  Support = -> [Pocket017]
  sketch-geometry (49):
    g0: LineSegment StartX=64.55 StartY=69.5497 StartZ=0 EndX=82.55 EndY=69.5497 EndZ=0
    g1: LineSegment StartX=82.55 StartY=69.5497 StartZ=0 EndX=82.55 EndY=66.3497 EndZ=0
    g2: LineSegment StartX=82.55 StartY=66.3497 StartZ=0 EndX=64.55 EndY=66.3497 EndZ=0
    g3: LineSegment StartX=64.55 StartY=66.3497 StartZ=0 EndX=64.55 EndY=69.5497 EndZ=0
    g4: LineSegment StartX=64.55 StartY=63.3497 StartZ=0 EndX=82.55 EndY=63.3497 EndZ=0
    g5: LineSegment StartX=82.55 StartY=63.3497 StartZ=0 EndX=82.55 EndY=60.1497 EndZ=0
    g6: LineSegment StartX=82.55 StartY=60.1497 StartZ=0 EndX=64.55 EndY=60.1497 EndZ=0
    g7: LineSegment StartX=64.55 StartY=60.1497 StartZ=0 EndX=64.55 EndY=63.3497 EndZ=0
    g8: LineSegment StartX=64.55 StartY=57.1497 StartZ=0 EndX=82.55 EndY=57.1497 EndZ=0
    g9: LineSegment StartX=82.55 StartY=57.1497 StartZ=0 EndX=82.55 EndY=53.9497 EndZ=0
    g10: LineSegment StartX=82.55 StartY=53.9497 StartZ=0 EndX=64.55 EndY=53.9497 EndZ=0
    g11: LineSegment StartX=64.55 StartY=53.9497 StartZ=0 EndX=64.55 EndY=57.1497 EndZ=0
    g12: LineSegment StartX=64.3277 StartY=50.9497 StartZ=0 EndX=82.3277 EndY=50.9497 EndZ=0
    g13: LineSegment StartX=82.3277 StartY=50.9497 StartZ=0 EndX=82.3277 EndY=47.7497 EndZ=0
    g14: LineSegment StartX=82.3277 StartY=47.7497 StartZ=0 EndX=64.3277 EndY=47.7497 EndZ=0
    g15: LineSegment StartX=64.3277 StartY=47.7497 StartZ=0 EndX=64.3277 EndY=50.9497 EndZ=0
    g16: LineSegment StartX=64.55 StartY=44.7497 StartZ=0 EndX=82.55 EndY=44.7497 EndZ=0
    g17: LineSegment StartX=82.55 StartY=44.7497 StartZ=0 EndX=82.55 EndY=41.5497 EndZ=0
    g18: LineSegment StartX=64.55 StartY=41.5497 StartZ=0 EndX=64.55 EndY=44.7497 EndZ=0
    g19: LineSegment StartX=64.55 StartY=38.5497 StartZ=0 EndX=82.55 EndY=38.5497 EndZ=0
    g20: LineSegment StartX=82.55 StartY=38.5497 StartZ=0 EndX=82.55 EndY=35.3497 EndZ=0
    g21: LineSegment StartX=82.55 StartY=35.3497 StartZ=0 EndX=64.55 EndY=35.3497 EndZ=0
    g22: LineSegment StartX=64.55 StartY=35.3497 StartZ=0 EndX=64.55 EndY=38.5497 EndZ=0
    g23: LineSegment [constr] StartX=99.55 StartY=41.0353 StartZ=0 EndX=99.55 EndY=66.5463 EndZ=0
    g24: LineSegment StartX=64.55 StartY=41.5497 StartZ=0 EndX=82.55 EndY=41.5497 EndZ=0
    g25: LineSegment StartX=134.55 StartY=69.5497 StartZ=0 EndX=116.55 EndY=69.5497 EndZ=0
    g26: LineSegment StartX=116.55 StartY=69.5497 StartZ=0 EndX=116.55 EndY=66.3497 EndZ=0
    g27: LineSegment StartX=116.55 StartY=66.3497 StartZ=0 EndX=134.55 EndY=66.3497 EndZ=0
    g28: LineSegment StartX=134.55 StartY=66.3497 StartZ=0 EndX=134.55 EndY=69.5497 EndZ=0
    g29: LineSegment StartX=134.55 StartY=63.3497 StartZ=0 EndX=116.55 EndY=63.3497 EndZ=0
    g30: LineSegment StartX=116.55 StartY=63.3497 StartZ=0 EndX=116.55 EndY=60.1497 EndZ=0
    g31: LineSegment StartX=116.55 StartY=60.1497 StartZ=0 EndX=134.55 EndY=60.1497 EndZ=0
    g32: LineSegment StartX=134.55 StartY=60.1497 StartZ=0 EndX=134.55 EndY=63.3497 EndZ=0
    g33: LineSegment StartX=134.55 StartY=57.1497 StartZ=0 EndX=116.55 EndY=57.1497 EndZ=0
    g34: LineSegment StartX=116.55 StartY=57.1497 StartZ=0 EndX=116.55 EndY=53.9497 EndZ=0
    g35: LineSegment StartX=116.55 StartY=53.9497 StartZ=0 EndX=134.55 EndY=53.9497 EndZ=0
    g36: LineSegment StartX=134.55 StartY=53.9497 StartZ=0 EndX=134.55 EndY=57.1497 EndZ=0
    g37: LineSegment StartX=134.772 StartY=50.9497 StartZ=0 EndX=116.772 EndY=50.9497 EndZ=0
    g38: LineSegment StartX=116.772 StartY=50.9497 StartZ=0 EndX=116.772 EndY=47.7497 EndZ=0
    g39: LineSegment StartX=116.772 StartY=47.7497 StartZ=0 EndX=134.772 EndY=47.7497 EndZ=0
    g40: LineSegment StartX=134.772 StartY=47.7497 StartZ=0 EndX=134.772 EndY=50.9497 EndZ=0
    g41: LineSegment StartX=134.55 StartY=44.7497 StartZ=0 EndX=116.55 EndY=44.7497 EndZ=0
    g42: LineSegment StartX=116.55 StartY=44.7497 StartZ=0 EndX=116.55 EndY=41.5497 EndZ=0
    g43: LineSegment StartX=134.55 StartY=41.5497 StartZ=0 EndX=134.55 EndY=44.7497 EndZ=0
    g44: LineSegment StartX=134.55 StartY=38.5497 StartZ=0 EndX=116.55 EndY=38.5497 EndZ=0
    g45: LineSegment StartX=116.55 StartY=38.5497 StartZ=0 EndX=116.55 EndY=35.3497 EndZ=0
    g46: LineSegment StartX=116.55 StartY=35.3497 StartZ=0 EndX=134.55 EndY=35.3497 EndZ=0
    g47: LineSegment StartX=134.55 StartY=35.3497 StartZ=0 EndX=134.55 EndY=38.5497 EndZ=0
    g48: LineSegment StartX=134.55 StartY=41.5497 StartZ=0 EndX=116.55 EndY=41.5497 EndZ=0
  constraints (123):
    c: Coincident(g0,g1)
    c: Coincident(g1,g2)
    c: Coincident(g2,g3)
    c: Coincident(g3,g0)
    c: Horizontal(g0)
    c: Horizontal(g2)
    c: Vertical(g1)
    c: Vertical(g3)
    c: Coincident(g4,g5)
    c: Coincident(g5,g6)
    c: Coincident(g6,g7)
    c: Coincident(g7,g4)
    c: Horizontal(g4)
    c: Horizontal(g6)
    c: Vertical(g5)
    c: Vertical(g7)
    c: Coincident(g8,g9)
    c: Coincident(g9,g10)
    c: Coincident(g10,g11)
    c: Coincident(g11,g8)
    c: Horizontal(g8)
    c: Horizontal(g10)
    c: Vertical(g9)
    c: Vertical(g11)
    c: Coincident(g12,g13)
    c: Coincident(g13,g14)
    c: Coincident(g14,g15)
    c: Coincident(g15,g12)
    c: Horizontal(g12)
    c: Horizontal(g14)
    c: Vertical(g13)
    c: Vertical(g15)
    c: Equal(g0,g4)
    c: Equal(g4,g8)
    c: Equal(g8,g12)
    c: Equal(g1,g5)
    c: Equal(g5,g9)
    c: Equal(g9,g13)
    c: DistanceY(g1,g1) = 3.2
    c: DistanceX(g0,g0) = 18
    c: DistanceY(g4,g2) = 3
    c: DistanceY(g8,g6) = 3
    c: DistanceY(g12,g10) = 3
    c: Coincident(g16,g17)
    c: Coincident(g18,g16)
    c: Horizontal(g16)
    c: Vertical(g17)
    c: Vertical(g18)
    c: Coincident(g19,g20)
    c: Coincident(g20,g21)
    c: Coincident(g21,g22)
    c: Coincident(g22,g19)
    c: Horizontal(g19)
    c: Horizontal(g21)
    c: Vertical(g20)
    c: Vertical(g22)
    c: Equal(g16,g12)
    c: Equal(g20,g17)
    c: Equal(g17,g13)
    c: DistanceY(g16,g14) = 3
    c: Coincident(g23,g-4)
    c: Vertical(g23)
    c: Coincident(g24,g18)
    c: Coincident(g24,g17)
    c: Horizontal(g24)
    c: DistanceY(g19,g18) = 3
    c: Coincident(g25,g26)
    c: Coincident(g26,g27)
    c: Coincident(g27,g28)
    c: Coincident(g28,g25)
    c: Horizontal(g25)
    c: Horizontal(g27)
    c: Vertical(g26)
    c: Vertical(g28)
    c: Coincident(g29,g30)
    c: Coincident(g30,g31)
    c: Coincident(g31,g32)
    c: Coincident(g32,g29)
    c: Horizontal(g29)
    c: Horizontal(g31)
    c: Vertical(g30)
    c: Vertical(g32)
    c: Coincident(g33,g34)
    c: Coincident(g34,g35)
    c: Coincident(g35,g36)
    c: Coincident(g36,g33)
    c: Horizontal(g33)
    c: Horizontal(g35)
    c: Vertical(g34)
    c: Vertical(g36)
    c: Coincident(g37,g38)
    c: Coincident(g38,g39)
    c: Coincident(g39,g40)
    c: Coincident(g40,g37)
    c: Horizontal(g37)
    c: Horizontal(g39)
    c: Vertical(g38)
    c: Vertical(g40)
    c: Equal(g25,g29)
    c: Equal(g29,g33)
    c: Equal(g33,g37)
    c: Equal(g26,g30)
    c: Equal(g30,g34)
    c: Equal(g34,g38)
    c: Coincident(g41,g42)
    c: Coincident(g43,g41)
    c: Horizontal(g41)
    c: Vertical(g42)
    c: Vertical(g43)
    c: Coincident(g44,g45)
    c: Coincident(g45,g46)
    c: Coincident(g46,g47)
    c: Coincident(g47,g44)
    c: Horizontal(g44)
    c: Horizontal(g46)
    c: Vertical(g45)
    c: Vertical(g47)
    c: Equal(g41,g37)
    c: Equal(g45,g42)
    c: Equal(g42,g38)
    c: Coincident(g48,g43)
    c: Coincident(g48,g42)
    c: Horizontal(g48)
FEATURE [PartDesign::Pocket] Pocket018
  BaseFeature = -> Pocket017
  Length = 5
  Length2 = 100
  Profile = -> Sketch043
  Refine = true
  Type = 0
FEATURE [Sketcher::SketchObject] Sketch044
  ExternalGeometry = -> [Pocket018]
  MapMode = 5
  Placement = pos=(0,62.55,0) rot=(1,0,0;1.5708rad)
  Support = -> [Pocket018]
  sketch-geometry (33):
    g0: LineSegment StartX=266 StartY=72 StartZ=0 EndX=269.2 EndY=72 EndZ=0
    g1: LineSegment StartX=269.2 StartY=72 StartZ=0 EndX=270.198 EndY=7 EndZ=0
    g2: LineSegment StartX=270.198 StartY=7 StartZ=0 EndX=266 EndY=7 EndZ=0
    g3: LineSegment StartX=266 StartY=7 StartZ=0 EndX=266 EndY=72 EndZ=0
    g4: LineSegment StartX=272.2 StartY=72 StartZ=0 EndX=275.4 EndY=72 EndZ=0
    g5: LineSegment StartX=275.4 StartY=72 StartZ=0 EndX=275.4 EndY=6.99233 EndZ=0
    g6: LineSegment StartX=275.4 StartY=6.99233 StartZ=0 EndX=272.2 EndY=6.99233 EndZ=0
    g7: LineSegment StartX=272.2 StartY=6.99233 StartZ=0 EndX=272.2 EndY=72 EndZ=0
    g8: LineSegment StartX=278.6 StartY=72 StartZ=0 EndX=281.6 EndY=72 EndZ=0
    g9: LineSegment StartX=281.6 StartY=72 StartZ=0 EndX=281.6 EndY=6.99233 EndZ=0
    g10: LineSegment StartX=281.6 StartY=6.99233 StartZ=0 EndX=278.6 EndY=6.99233 EndZ=0
    g11: LineSegment StartX=278.6 StartY=6.99233 StartZ=0 EndX=278.6 EndY=72 EndZ=0
    g12: LineSegment StartX=284.6 StartY=72 StartZ=0 EndX=287.6 EndY=72 EndZ=0
    g13: LineSegment StartX=287.6 StartY=72 StartZ=0 EndX=287.6 EndY=6.99233 EndZ=0
    g14: LineSegment StartX=287.6 StartY=6.99233 StartZ=0 EndX=284.6 EndY=6.99233 EndZ=0
    g15: LineSegment StartX=284.6 StartY=6.99233 StartZ=0 EndX=284.6 EndY=72 EndZ=0
    g16: LineSegment StartX=290.8 StartY=72 StartZ=0 EndX=293.8 EndY=72 EndZ=0
    g17: LineSegment StartX=293.8 StartY=72 StartZ=0 EndX=293.8 EndY=6.99233 EndZ=0
    g18: LineSegment StartX=293.8 StartY=6.99233 StartZ=0 EndX=290.8 EndY=6.99233 EndZ=0
    g19: LineSegment StartX=290.8 StartY=6.99233 StartZ=0 EndX=290.8 EndY=72 EndZ=0
    g20: LineSegment StartX=297 StartY=72 StartZ=0 EndX=300 EndY=72 EndZ=0
    g21: LineSegment StartX=300 StartY=72 StartZ=0 EndX=300 EndY=6.99233 EndZ=0
    g22: LineSegment StartX=300 StartY=6.99233 StartZ=0 EndX=297 EndY=6.99233 EndZ=0
    g23: LineSegment StartX=297 StartY=6.99233 StartZ=0 EndX=297 EndY=72 EndZ=0
    g24: LineSegment StartX=303.2 StartY=72 StartZ=0 EndX=306.2 EndY=72 EndZ=0
    g25: LineSegment StartX=306.2 StartY=72 StartZ=0 EndX=306.2 EndY=6.99233 EndZ=0
    g26: LineSegment StartX=306.2 StartY=6.99233 StartZ=0 EndX=303.2 EndY=6.99233 EndZ=0
    g27: LineSegment StartX=303.2 StartY=6.99233 StartZ=0 EndX=303.2 EndY=72 EndZ=0
    g28: LineSegment StartX=309.4 StartY=72 StartZ=0 EndX=312.4 EndY=72 EndZ=0
    g29: LineSegment StartX=312.4 StartY=72 StartZ=0 EndX=312.4 EndY=6.99233 EndZ=0
    g30: LineSegment StartX=312.4 StartY=6.99233 StartZ=0 EndX=309.4 EndY=6.99233 EndZ=0
    g31: LineSegment StartX=309.4 StartY=6.99233 StartZ=0 EndX=309.4 EndY=72 EndZ=0
    g32: LineSegment [constr] StartX=275.4 StartY=72 StartZ=0 EndX=330.145 EndY=72 EndZ=0
  constraints (97):
    c: Coincident(g0,g1)
    c: Coincident(g1,g2)
    c: Coincident(g2,g3)
    c: Coincident(g3,g0)
    c: Horizontal(g0)
    c: Horizontal(g2)
    c: Vertical(g3)
    c: DistanceX(g-3,g0) = 2
    c: DistanceY(g0,g-3) = 3
    c: DistanceX(g0,g0) = 3.2
    c: Coincident(g4,g5)
    c: Coincident(g5,g6)
    c: Coincident(g6,g7)
    c: Coincident(g7,g4)
    c: Horizontal(g4)
    c: Horizontal(g6)
    c: Vertical(g5)
    c: Vertical(g7)
    c: DistanceY(g1,g1) = 65
    c: Equal(g1,g7)
    c: Equal(g0,g4)
    c: DistanceY(g4,g-3) = 3
    c: DistanceX(g0,g4) = 3
    c: Coincident(g8,g9)
    c: Coincident(g9,g10)
    c: Coincident(g10,g11)
    c: Coincident(g11,g8)
    c: Horizontal(g8)
    c: Horizontal(g10)
    c: Vertical(g9)
    c: Vertical(g11)
    c: Coincident(g12,g13)
    c: Coincident(g13,g14)
    c: Coincident(g14,g15)
    c: Coincident(g15,g12)
    c: Horizontal(g12)
    c: Horizontal(g14)
    c: Vertical(g13)
    c: Vertical(g15)
    c: Coincident(g16,g17)
    c: Coincident(g17,g18)
    c: Coincident(g18,g19)
    c: Coincident(g19,g16)
    c: Horizontal(g16)
    c: Horizontal(g18)
    c: Vertical(g17)
    c: Vertical(g19)
    c: Coincident(g20,g21)
    c: Coincident(g21,g22)
    c: Coincident(g22,g23)
    c: Coincident(g23,g20)
    c: Horizontal(g20)
    c: Horizontal(g22)
    c: Vertical(g21)
    c: Vertical(g23)
    c: Coincident(g24,g25)
    c: Coincident(g25,g26)
    c: Coincident(g26,g27)
    c: Coincident(g27,g24)
    c: Horizontal(g24)
    c: Horizontal(g26)
    c: Vertical(g25)
    c: Vertical(g27)
    c: Coincident(g28,g29)
    c: Coincident(g29,g30)
    c: Coincident(g30,g31)
    c: Coincident(g31,g28)
    c: Horizontal(g28)
    c: Horizontal(g30)
    c: Vertical(g29)
    c: Vertical(g31)
    c: DistanceX(g8,g8) = 3
    c: Equal(g28,g24)
    c: Equal(g24,g20)
    c: Equal(g20,g16)
    c: Equal(g16,g12)
    c: Equal(g12,g8)
    c: Equal(g5,g9)
    c: Equal(g9,g15)
    c: Equal(g15,g19)
    c: Equal(g19,g23)
    c: Equal(g23,g27)
    c: Equal(g27,g31)
    c: DistanceX(g12,g16) = 3.2
    c: DistanceX(g16,g20) = 3.2
    c: DistanceX(g20,g24) = 3.2
    c: DistanceX(g24,g28) = 3.2
    c: DistanceX(g4,g8) = 3.2
    c: DistanceX(g8,g12) = 3
    c: Coincident(g32,g4)
    c: Horizontal(g32)
    c: PointOnObject(g8,g32)
    c: PointOnObject(g12,g32)
    c: PointOnObject(g16,g32)
    c: PointOnObject(g20,g32)
    c: PointOnObject(g24,g32)
    c: PointOnObject(g28,g32)
FEATURE [PartDesign::Pocket] Pocket019
  BaseFeature = -> Pocket018
  Length = 5
  Length2 = 100
  Profile = -> Sketch044
  Refine = true
  Type = 1
FEATURE [Sketcher::SketchObject] Sketch045
  MapMode = 5
  Support = -> [XY_Plane011]
  sketch-geometry (2):
    g0: Circle CenterX=0 CenterY=-30.9347 CenterZ=0 NormalX=0 NormalY=0 NormalZ=1 AngleXU=0 Radius=1.75
    g1: Circle CenterX=0 CenterY=-30.9347 CenterZ=0 NormalX=0 NormalY=0 NormalZ=1 AngleXU=0 Radius=3
  constraints (4):
    c: PointOnObject(g0,g-2)
    c: Coincident(g1,g0)
    c: Diameter(g0) = 3.5
    c: Diameter(g1) = 6
FEATURE [PartDesign::Pad] Pad025
  Length = 10
  Length2 = 100
  Profile = -> Sketch045
  Refine = true
  Type = 0
FEATURE [PartDesign::Body] Body011  label="separador"
  Group = -> [Sketch045,Pad025]
  Origin = -> Origin011
  Tip = -> Pad025
FEATURE [Sketcher::SketchObject] Sketch046
  ExternalGeometry = -> [Pocket016]
  MapMode = 5
  Placement = pos=(0,0,5) rot=(0,0,1;0rad)
  Support = -> [Pocket016]
  sketch-geometry (5):
    g0: Circle CenterX=65.384 CenterY=248.554 CenterZ=0 NormalX=0 NormalY=0 NormalZ=1 AngleXU=0 Radius=1.6
    g1: LineSegment [constr] StartX=100.384 StartY=209.304 StartZ=0 EndX=100.384 EndY=268.312 EndZ=0
    g2: Circle CenterX=135.384 CenterY=248.554 CenterZ=0 NormalX=0 NormalY=0 NormalZ=1 AngleXU=0 Radius=1.6
    g3: LineSegment [constr] StartX=100.384 StartY=209.304 StartZ=0 EndX=100.384 EndY=143.095 EndZ=0
    g4: Circle CenterX=100.384 CenterY=173.554 CenterZ=0 NormalX=0 NormalY=0 NormalZ=1 AngleXU=0 Radius=1.6
  constraints (11):
    c: Diameter(g0) = 3.2
    c: DistanceX(g-3,g0) = 15
    c: DistanceY(g0,g-3) = 15
    c: Coincident(g1,g-4)
    c: Vertical(g1)
    c: Diameter(g2) = 3.2
    c: Coincident(g3,g1)
    c: Vertical(g3)
    c: PointOnObject(g4,g3)
    c: Diameter(g4) = 3.2
    c: DistanceY(g-5,g4) = 10
FEATURE [PartDesign::Pocket] Pocket020
  BaseFeature = -> Pocket016
  Length = 5
  Length2 = 100
  Profile = -> Sketch046
  Refine = true
  Type = 0
FEATURE [PartDesign::Body] Body010  label="soporte-tubo-inferior"
  Group = -> [Sketch039,Pad023,Sketch040,Pad024,DatumPlane002,Sketch041,Pocket016,Sketch046,Pocket020]
  Origin = -> Origin010
  Tip = -> Pocket020
FEATURE [Part::FeaturePython] Clone017  label="soporte-tubo-inferior-e"  # Draft clone (typed FeaturePython)
  AttacherType = Attacher::AttachEngine3D
  Fuse = false
  Objects = -> [Pocket020]
  Placement = pos=(-100.5,-163.5,100) rot=(0,0,1;0rad)
  Scale = (1,1,1)
FEATURE [Part::FeaturePython] Clone019  label="caja-sensores-e"  # Draft clone (typed FeaturePython)
  AttacherType = Attacher::AttachEngine3D
  Fuse = false
  Objects = -> [LinearPattern]
  Placement = pos=(47,-54.5,152) rot=(0,-1,0;1.5708rad)
  Scale = (1,1,1)
FEATURE [Sketcher::SketchObject] Sketch052
  ExternalGeometry = -> [Pocket019]
  MapMode = 5
  Placement = pos=(320,0,0) rot=(0.57735,0.57735,0.57735;2.0944rad)
  Support = -> [Pocket019]
  sketch-geometry (5):
    g0: LineSegment StartX=73.55 StartY=14.0475 StartZ=0 EndX=73.55 EndY=-1.92886 EndZ=0
    g1: LineSegment StartX=73.55 StartY=-1.92886 StartZ=0 EndX=65.55 EndY=-1.92886 EndZ=0
    g2: LineSegment StartX=65.55 StartY=-1.92886 StartZ=0 EndX=65.55 EndY=4.51346 EndZ=0
    g3: ArcOfCircle CenterX=81.2134 CenterY=-0.506264 CenterZ=0 NormalX=0 NormalY=0 NormalZ=1 AngleXU=0 Radius=16.4481 StartAngle=2.05546 EndAngle=2.83146
    g4: LineSegment [constr] StartX=65.55 StartY=4.51346 StartZ=0 EndX=73.55 EndY=14.0475 EndZ=0
  constraints (12):
    c: Coincident(g0,g1)
    c: Coincident(g1,g2)
    c: Horizontal(g1)
    c: Vertical(g0)
    c: Vertical(g2)
    c: DistanceX(g-3,g1) = 8
    c: Coincident(g2,g3)
    c: Coincident(g3,g0)
    c: DistanceX(g2,g0) = 8
    c: Coincident(g4,g2)
    c: Coincident(g4,g0)
    c: Angle(g-3,g4) = 0.872665
FEATURE [PartDesign::Pocket] Pocket024
  BaseFeature = -> Pocket019
  Length = 5
  Length2 = 100
  Profile = -> Sketch052
  Refine = true
  Type = 0
FEATURE [Part::FeaturePython] Clone021  label="verde-e"  # Draft clone (typed FeaturePython)
  AttacherType = Attacher::AttachEngine3D
  Fuse = false
  Objects = -> [Pocket]
  Placement = pos=(46,45.5,517) rot=(0.707107,0,-0.707107;3.14159rad)
  Scale = (1,1,1)
FEATURE [Part::FeaturePython] Clone022  label="amarillo-e"  # Draft clone (typed FeaturePython)
  AttacherType = Attacher::AttachEngine3D
  Fuse = false
  Objects = -> [Pocket001]
  Placement = pos=(46,45.5,702) rot=(0.707107,0,-0.707107;3.14159rad)
  Scale = (1,1,1)
FEATURE [Part::FeaturePython] Clone023  label="rojo-e"  # Draft clone (typed FeaturePython)
  AttacherType = Attacher::AttachEngine3D
  Fuse = false
  Objects = -> [Pocket002]
  Placement = pos=(46,45.5,882) rot=(0.707107,0,-0.707107;3.14159rad)
  Scale = (1,1,1)
FEATURE [Part::FeaturePython] Clone025  label="soporte-tubo-superior-e"  # Draft clone (typed FeaturePython)
  AttacherType = Attacher::AttachEngine3D
  Fuse = false
  Objects = -> [Pocket003]
  Placement = pos=(107,-54.5,312) rot=(0,1,0;3.14159rad)
  Scale = (1,1,1)
FEATURE [Part::FeaturePython] Clone015  label="separador-e"  # Draft clone (typed FeaturePython)
  AttacherType = Attacher::AttachEngine3D
  Fuse = false
  Objects = -> [Body011]
  Placement = pos=(-43.5,80,351) rot=(0,1,0;1.5708rad)
  Scale = (1,1,1)
FEATURE [Sketcher::SketchObject] Sketch053
  MapMode = 5
  Support = -> [XY_Plane013]
  sketch-geometry (4):
    g0: LineSegment StartX=-160.581 StartY=227.341 StartZ=0 EndX=-100.981 EndY=227.341 EndZ=0
    g1: LineSegment StartX=-100.981 StartY=227.341 StartZ=0 EndX=-100.981 EndY=203.341 EndZ=0
    g2: LineSegment StartX=-100.981 StartY=203.341 StartZ=0 EndX=-160.581 EndY=203.341 EndZ=0
    g3: LineSegment StartX=-160.581 StartY=203.341 StartZ=0 EndX=-160.581 EndY=227.341 EndZ=0
  constraints (10):
    c: Coincident(g0,g1)
    c: Coincident(g1,g2)
    c: Coincident(g2,g3)
    c: Horizontal(g0)
    c: Horizontal(g2)
    c: Vertical(g1)
    c: Vertical(g3)
    c: DistanceY(g3,g0) = 24
    c: DistanceX(g0,g0) = 59.6
    c: Coincident(g3,g0)
FEATURE [PartDesign::Pad] Pad028
  Length = 22
  Length2 = 100
  Profile = -> Sketch053
  Refine = true
  Type = 0
FEATURE [Sketcher::SketchObject] Sketch054
  ExternalGeometry = -> [Pad028]
  MapMode = 5
  Placement = pos=(0,0,0) rot=(1,0,0;3.14159rad)
  Support = -> [Pad028]
  sketch-geometry (4):
    g0: LineSegment StartX=-162.581 StartY=-210.341 StartZ=0 EndX=-152.581 EndY=-210.341 EndZ=0
    g1: LineSegment StartX=-152.581 StartY=-210.341 StartZ=0 EndX=-152.581 EndY=-220.341 EndZ=0
    g2: LineSegment StartX=-152.581 StartY=-220.341 StartZ=0 EndX=-162.581 EndY=-220.341 EndZ=0
    g3: LineSegment StartX=-162.581 StartY=-220.341 StartZ=0 EndX=-162.581 EndY=-210.341 EndZ=0
  constraints (13):
    c: Coincident(g0,g1)
    c: Coincident(g1,g2)
    c: Coincident(g2,g3)
    c: Coincident(g3,g0)
    c: Horizontal(g0)
    c: Horizontal(g2)
    c: Vertical(g1)
    c: Vertical(g3)
    c: DistanceY(g1,g1) = 10
    c: DistanceY(g-4,g-4) = 24
    c: DistanceY(g0,g-4) = 7
    c: DistanceX(g0,g0) = 10
    c: DistanceX(g2,g-4) = 2
FEATURE [PartDesign::Pocket] Pocket025
  BaseFeature = -> Pad028
  Length = 6
  Length2 = 100
  Profile = -> Sketch054
  Refine = true
  Type = 0
FEATURE [Sketcher::SketchObject] Sketch055
  ExternalGeometry = -> [Pocket025]
  MapMode = 5
  Placement = pos=(0,0,22) rot=(0,0,1;0rad)
  Support = -> [Pocket025]
  sketch-geometry (4):
    g0: LineSegment StartX=-122.981 StartY=219.341 StartZ=0 EndX=-114.981 EndY=219.341 EndZ=0
    g1: LineSegment StartX=-114.981 StartY=219.341 StartZ=0 EndX=-114.981 EndY=211.341 EndZ=0
    g2: LineSegment StartX=-114.981 StartY=211.341 StartZ=0 EndX=-122.981 EndY=211.341 EndZ=0
    g3: LineSegment StartX=-122.981 StartY=211.341 StartZ=0 EndX=-122.981 EndY=219.341 EndZ=0
  constraints (12):
    c: Coincident(g0,g1)
    c: Coincident(g1,g2)
    c: Coincident(g2,g3)
    c: Coincident(g3,g0)
    c: Horizontal(g0)
    c: Horizontal(g2)
    c: Vertical(g1)
    c: Vertical(g3)
    c: DistanceY(g3,g3) = 8
    c: DistanceX(g0,g0) = 8
    c: DistanceY(g-3,g1) = 8
    c: DistanceX(g0,g-3) = 14
FEATURE [PartDesign::Pocket] Pocket026
  BaseFeature = -> Pocket025
  Length = 9
  Length2 = 100
  Profile = -> Sketch055
  Refine = true
  Type = 0
FEATURE [Sketcher::SketchObject] Sketch056
  ExternalGeometry = -> [Pocket026]
  MapMode = 5
  Placement = pos=(-160.581,0,0) rot=(0.57735,-0.57735,-0.57735;2.0944rad)
  Support = -> [Pocket026]
  sketch-geometry (4):
    g0: LineSegment StartX=-225.841 StartY=16 StartZ=0 EndX=-204.841 EndY=16 EndZ=0
    g1: LineSegment StartX=-204.841 StartY=16 StartZ=0 EndX=-204.841 EndY=4 EndZ=0
    g2: LineSegment StartX=-204.841 StartY=4 StartZ=0 EndX=-225.841 EndY=4 EndZ=0
    g3: LineSegment StartX=-225.841 StartY=4 StartZ=0 EndX=-225.841 EndY=16 EndZ=0
  constraints (12):
    c: Coincident(g0,g1)
    c: Coincident(g1,g2)
    c: Coincident(g2,g3)
    c: Coincident(g3,g0)
    c: Horizontal(g0)
    c: Horizontal(g2)
    c: Vertical(g1)
    c: Vertical(g3)
    c: DistanceY(g-4,g2) = 4
    c: DistanceY(g0,g-4) = 6
    c: DistanceX(g-4,g0) = 1.5
    c: DistanceX(g0,g-5) = 1.5
FEATURE [PartDesign::Pocket] Pocket027
  BaseFeature = -> Pocket026
  Length = 56
  Length2 = 100
  Profile = -> Sketch056
  Refine = true
  Type = 0
FEATURE [Sketcher::SketchObject] Sketch057
  ExternalGeometry = -> [Pocket027]
  MapMode = 5
  Placement = pos=(0,0,22) rot=(0,0,1;0rad)
  Support = -> [Pocket027]
  sketch-geometry (1):
    g0: Circle CenterX=-130.781 CenterY=215.341 CenterZ=0 NormalX=0 NormalY=0 NormalZ=1 AngleXU=0 Radius=1.75
  constraints (3):
    c: Diameter(g0) = 3.5
    c: DistanceY(g0,g-3) = 12
    c: DistanceX(g0,g-3) = 29.8
FEATURE [PartDesign::Pocket] Pocket028
  BaseFeature = -> Pocket027
  Length = 5
  Length2 = 100
  Profile = -> Sketch057
  Refine = true
  Type = 1
FEATURE [PartDesign::Chamfer] Chamfer002
  Base = -> Pocket028 [Edge43,Edge42,Edge44,Edge45]
  BaseFeature = -> Pocket028
  Size = 3
FEATURE [Sketcher::SketchObject] Sketch058
  ExternalGeometry = -> [Chamfer002]
  MapMode = 5
  Placement = pos=(0,0,22) rot=(0,0,1;0rad)
  Support = -> [Chamfer002]
  sketch-geometry (1):
    g0: Circle CenterX=-130.781 CenterY=215.341 CenterZ=0 NormalX=0 NormalY=0 NormalZ=1 AngleXU=0 Radius=2.85
  constraints (2):
    c: Coincident(g0,g-3)
    c: Diameter(g0) = 5.7
FEATURE [PartDesign::Pocket] Pocket029
  BaseFeature = -> Chamfer002
  Length = 3
  Length2 = 100
  Profile = -> Sketch058
  Refine = true
  Type = 0
FEATURE [Sketcher::SketchObject] Sketch059
  ExternalGeometry = -> [Pocket029]
  MapMode = 5
  Placement = pos=(0,0,0) rot=(1,0,0;3.14159rad)
  Support = -> [Pocket029]
  sketch-geometry (7):
    g0: LineSegment StartX=-127.663 StartY=-217.141 StartZ=0 EndX=-127.663 EndY=-213.541 EndZ=0
    g1: LineSegment StartX=-127.663 StartY=-213.541 StartZ=0 EndX=-130.781 EndY=-211.741 EndZ=0
    g2: LineSegment StartX=-130.781 StartY=-211.741 StartZ=0 EndX=-133.899 EndY=-213.541 EndZ=0
    g3: LineSegment StartX=-133.899 StartY=-213.541 StartZ=0 EndX=-133.899 EndY=-217.141 EndZ=0
    g4: LineSegment StartX=-133.899 StartY=-217.141 StartZ=0 EndX=-130.781 EndY=-218.941 EndZ=0
    g5: LineSegment StartX=-130.781 StartY=-218.941 StartZ=0 EndX=-127.663 EndY=-217.141 EndZ=0
    g6: Circle [constr] CenterX=-130.781 CenterY=-215.341 CenterZ=0 NormalX=0 NormalY=0 NormalZ=1 AngleXU=0 Radius=3.6
  constraints (16):
    c: Coincident(g0,g1)
    c: Coincident(g1,g2)
    c: Coincident(g2,g3)
    c: Coincident(g3,g4)
    c: Coincident(g4,g5)
    c: Coincident(g5,g0)
    c: Equal(g0, g1-g5) x5
    c: PointOnObject(g0,g6)
    c: PointOnObject(g1,g6)
    c: PointOnObject(g2,g6)
    c: PointOnObject(g3,g6)
    c: PointOnObject(g4,g6)
    c: PointOnObject(g5,g6)
    c: Coincident(g6,g-3)
    c: Vertical(g0)
    c: Diameter(g6) = 7.2
FEATURE [PartDesign::Pocket] Pocket030
  BaseFeature = -> Pocket029
  Length = 2.5
  Length2 = 100
  Profile = -> Sketch059
  Refine = true
  Type = 0
FEATURE [PartDesign::Body] Body013  label="caja-CCS811"
  Group = -> [Sketch053,Pad028,Sketch054,Pocket025,Sketch055,Pocket026,Sketch056,Pocket027,Sketch057,Pocket028,Chamfer002,Sketch058,Pocket029,Sketch059,Pocket030]
  Origin = -> Origin013
  Tip = -> Pocket030
FEATURE [Part::FeaturePython] Clone027  label="caja-CCS811-e"  # Draft clone (typed FeaturePython)
  AttacherType = Attacher::AttachEngine3D
  Fuse = false
  Objects = -> [Body013]
  Placement = pos=(-50,291,211) rot=(0.707107,0,-0.707107;3.14159rad)
  Scale = (1,1,1)
FEATURE [Sketcher::SketchObject] Sketch060
  MapMode = 5
  Support = -> [XY_Plane014]
  sketch-geometry (4):
    g0: LineSegment StartX=-143.473 StartY=193.074 StartZ=0 EndX=-119.473 EndY=193.074 EndZ=0
    g1: LineSegment StartX=-119.473 StartY=193.074 StartZ=0 EndX=-119.473 EndY=171.074 EndZ=0
    g2: LineSegment StartX=-119.473 StartY=171.074 StartZ=0 EndX=-143.473 EndY=171.074 EndZ=0
    g3: LineSegment StartX=-143.473 StartY=171.074 StartZ=0 EndX=-143.473 EndY=193.074 EndZ=0
  constraints (10):
    c: Coincident(g0,g1)
    c: Coincident(g1,g2)
    c: Coincident(g2,g3)
    c: Coincident(g3,g0)
    c: Horizontal(g0)
    c: Horizontal(g2)
    c: Vertical(g1)
    c: Vertical(g3)
    c: DistanceX(g0,g0) = 24
    c: DistanceY(g1,g1) = 22
FEATURE [PartDesign::Pad] Pad029
  Length = 0.5
  Length2 = 100
  Profile = -> Sketch060
  Refine = true
  Type = 0
FEATURE [Sketcher::SketchObject] Sketch061
  ExternalGeometry = -> [Pad029]
  MapMode = 5
  Placement = pos=(0,0,0.5) rot=(0,0,1;0rad)
  Support = -> [Pad029]
  sketch-geometry (8):
    g0: LineSegment [constr] StartX=-141.973 StartY=188.074 StartZ=0 EndX=-120.973 EndY=188.074 EndZ=0
    g1: LineSegment [constr] StartX=-120.973 StartY=188.074 StartZ=0 EndX=-120.973 EndY=176.074 EndZ=0
    g2: LineSegment [constr] StartX=-120.973 StartY=176.074 StartZ=0 EndX=-141.973 EndY=176.074 EndZ=0
    g3: LineSegment [constr] StartX=-141.973 StartY=176.074 StartZ=0 EndX=-141.973 EndY=188.074 EndZ=0
    g4: LineSegment StartX=-141.923 StartY=188.024 StartZ=0 EndX=-121.023 EndY=188.024 EndZ=0
    g5: LineSegment StartX=-121.023 StartY=188.024 StartZ=0 EndX=-121.023 EndY=176.124 EndZ=0
    g6: LineSegment StartX=-121.023 StartY=176.124 StartZ=0 EndX=-141.923 EndY=176.124 EndZ=0
    g7: LineSegment StartX=-141.923 StartY=176.124 StartZ=0 EndX=-141.923 EndY=188.024 EndZ=0
  constraints (24):
    c: Coincident(g0,g1)
    c: Coincident(g1,g2)
    c: Coincident(g2,g3)
    c: Coincident(g3,g0)
    c: Horizontal(g0)
    c: Horizontal(g2)
    c: Vertical(g1)
    c: Vertical(g3)
    c: DistanceX(g0,g0) = 21
    c: DistanceY(g1,g1) = 12
    c: DistanceX(g-3,g0) = 1.5
    c: DistanceY(g-4,g1) = 5
    c: Coincident(g4,g5)
    c: Coincident(g5,g6)
    c: Coincident(g6,g7)
    c: Coincident(g7,g4)
    c: Horizontal(g4)
    c: Horizontal(g6)
    c: Vertical(g5)
    c: Vertical(g7)
    c: DistanceY(g4,g0) = 0.05
    c: DistanceY(g1,g5) = 0.05
    c: DistanceX(g4,g0) = 0.05
    c: DistanceX(g2,g6) = 0.05
FEATURE [PartDesign::Pad] Pad030
  BaseFeature = -> Pad029
  Length = 0.5
  Length2 = 100
  Profile = -> Sketch061
  Refine = true
  Type = 0
FEATURE [Sketcher::SketchObject] Sketch062
  ExternalGeometry = -> [Pad030]
  MapMode = 5
  Placement = pos=(0,0,1) rot=(0,0,1;0rad)
  Support = -> [Pad030]
  sketch-geometry (10):
    g0: Circle CenterX=-138.816 CenterY=184.7 CenterZ=0 NormalX=0 NormalY=0 NormalZ=1 AngleXU=0 Radius=1.5
    g1: LineSegment [constr] StartX=-138.816 StartY=184.7 StartZ=0 EndX=-123.816 EndY=184.7 EndZ=0
    g2: Circle CenterX=-133.816 CenterY=184.7 CenterZ=0 NormalX=0 NormalY=0 NormalZ=1 AngleXU=0 Radius=1.5
    g3: Circle CenterX=-128.816 CenterY=184.7 CenterZ=0 NormalX=0 NormalY=0 NormalZ=1 AngleXU=0 Radius=1.5
    g4: Circle CenterX=-123.816 CenterY=184.7 CenterZ=0 NormalX=0 NormalY=0 NormalZ=1 AngleXU=0 Radius=1.5
    g5: LineSegment [constr] StartX=-141.923 StartY=182.124 StartZ=0 EndX=-115.93 EndY=182.124 EndZ=0
    g6: Circle CenterX=-138.816 CenterY=179.447 CenterZ=0 NormalX=0 NormalY=0 NormalZ=1 AngleXU=0 Radius=1.5
    g7: Circle CenterX=-133.816 CenterY=179.447 CenterZ=0 NormalX=0 NormalY=0 NormalZ=1 AngleXU=0 Radius=1.5
    g8: Circle CenterX=-128.816 CenterY=179.447 CenterZ=0 NormalX=0 NormalY=0 NormalZ=1 AngleXU=0 Radius=1.5
    g9: Circle CenterX=-123.816 CenterY=179.447 CenterZ=0 NormalX=0 NormalY=0 NormalZ=1 AngleXU=0 Radius=1.5
  constraints (21):
    c: Diameter(g0) = 3
    c: DistanceX(g-4,g-4) = 20.9
    c: DistanceY(g-3,g-3) = 11.9
    c: Coincident(g1,g0)
    c: Horizontal(g1)
    c: Equal(g2,g0)
    c: DistanceX(g0,g2) = 5
    c: PointOnObject(g3,g1)
    c: Equal(g3,g4)
    c: Equal(g4,g2)
    c: DistanceX(g2,g3) = 5
    c: DistanceX(g3,g4) = 5
    c: Coincident(g1,g4)
    c: PointOnObject(g2,g1)
    c: PointOnObject(g5,g-3)
    c: Horizontal(g5)
    c: DistanceY(g5,g-4) = 5.9
    c: Diameter(g6) = 3
    c: Equal(g7,g6)
    c: Equal(g8,g9)
    c: Equal(g9,g7)
FEATURE [PartDesign::Pocket] Pocket031
  BaseFeature = -> Pad030
  Length = 5
  Length2 = 100
  Profile = -> Sketch062
  Refine = true
  Type = 0
FEATURE [Sketcher::SketchObject] Sketch063
  ExternalGeometry = -> [Pocket031]
  MapMode = 5
  Placement = pos=(0,0,1) rot=(0,0,1;0rad)
  Support = -> [Pocket031]
  sketch-geometry (26):
    g0: LineSegment StartX=-141.923 StartY=188.024 StartZ=0 EndX=-137.923 EndY=188.024 EndZ=0
    g1: LineSegment StartX=-137.923 StartY=188.024 StartZ=0 EndX=-137.923 EndY=187.024 EndZ=0
    g2: LineSegment StartX=-137.923 StartY=187.024 StartZ=0 EndX=-140.923 EndY=187.024 EndZ=0
    g3: LineSegment StartX=-140.923 StartY=187.024 StartZ=0 EndX=-140.923 EndY=184.024 EndZ=0
    g4: LineSegment StartX=-140.923 StartY=184.024 StartZ=0 EndX=-141.923 EndY=184.024 EndZ=0
    g5: LineSegment StartX=-141.923 StartY=184.024 StartZ=0 EndX=-141.923 EndY=188.024 EndZ=0
    g6: LineSegment [constr] StartX=-131.473 StartY=188.024 StartZ=0 EndX=-131.473 EndY=176.124 EndZ=0
    g7: LineSegment [constr] StartX=-141.923 StartY=182.074 StartZ=0 EndX=-121.023 EndY=182.074 EndZ=0
    g8: LineSegment StartX=-121.023 StartY=188.024 StartZ=0 EndX=-125.023 EndY=188.024 EndZ=0
    g9: LineSegment StartX=-125.023 StartY=188.024 StartZ=0 EndX=-125.023 EndY=187.024 EndZ=0
    g10: LineSegment StartX=-125.023 StartY=187.024 StartZ=0 EndX=-122.023 EndY=187.024 EndZ=0
    g11: LineSegment StartX=-122.023 StartY=187.024 StartZ=0 EndX=-122.023 EndY=184.024 EndZ=0
    g12: LineSegment StartX=-122.023 StartY=184.024 StartZ=0 EndX=-121.023 EndY=184.024 EndZ=0
    g13: LineSegment StartX=-121.023 StartY=184.024 StartZ=0 EndX=-121.023 EndY=188.024 EndZ=0
    g14: LineSegment StartX=-141.923 StartY=176.124 StartZ=0 EndX=-137.923 EndY=176.124 EndZ=0
    g15: LineSegment StartX=-137.923 StartY=176.124 StartZ=0 EndX=-137.923 EndY=177.124 EndZ=0
    g16: LineSegment StartX=-137.923 StartY=177.124 StartZ=0 EndX=-140.923 EndY=177.124 EndZ=0
    g17: LineSegment StartX=-140.923 StartY=177.124 StartZ=0 EndX=-140.923 EndY=180.124 EndZ=0
    g18: LineSegment StartX=-140.923 StartY=180.124 StartZ=0 EndX=-141.923 EndY=180.124 EndZ=0
    g19: LineSegment StartX=-141.923 StartY=180.124 StartZ=0 EndX=-141.923 EndY=176.124 EndZ=0
    g20: LineSegment StartX=-121.023 StartY=176.124 StartZ=0 EndX=-125.023 EndY=176.124 EndZ=0
    g21: LineSegment StartX=-125.023 StartY=176.124 StartZ=0 EndX=-125.023 EndY=177.124 EndZ=0
    g22: LineSegment StartX=-125.023 StartY=177.124 StartZ=0 EndX=-122.023 EndY=177.124 EndZ=0
    g23: LineSegment StartX=-122.023 StartY=177.124 StartZ=0 EndX=-122.023 EndY=180.124 EndZ=0
    g24: LineSegment StartX=-122.023 StartY=180.124 StartZ=0 EndX=-121.023 EndY=180.124 EndZ=0
    g25: LineSegment StartX=-121.023 StartY=180.124 StartZ=0 EndX=-121.023 EndY=176.124 EndZ=0
  constraints (68):
    c: Coincident(g0,g1)
    c: Coincident(g1,g2)
    c: Horizontal(g0)
    c: Horizontal(g2)
    c: Vertical(g1)
    c: Coincident(g3,g4)
    c: Coincident(g4,g5)
    c: Horizontal(g4)
    c: Vertical(g3)
    c: Vertical(g5)
    c: Equal(g1,g4)
    c: DistanceY(g1,g1) = 1
    c: Coincident(g2,g3)
    c: Equal(g3,g2)
    c: DistanceX(g2,g2) = 3
    c: Coincident(g5,g0)
    c: Coincident(g0,g-3)
    c: PointOnObject(g6,g-3)
    c: PointOnObject(g6,g-4)
    c: Vertical(g6)
    c: Horizontal(g7)
    c: DistanceX(g6,g-3) = 10.45
    c: PointOnObject(g7,g-5)
    c: PointOnObject(g7,g-6)
    c: DistanceY(g-5,g-5) = 11.9
    c: DistanceY(g7,g-5) = 5.95
    c: Coincident(g8,g9)
    c: Coincident(g9,g10)
    c: Horizontal(g8)
    c: Horizontal(g10)
    c: Vertical(g9)
    c: Coincident(g11,g12)
    c: Coincident(g12,g13)
    c: Horizontal(g12)
    c: Vertical(g11)
    c: Vertical(g13)
    c: Equal(g9,g12)
    c: Coincident(g10,g11)
    c: Equal(g11,g10)
    c: Coincident(g13,g8)
    c: Coincident(g14,g15)
    c: Coincident(g15,g16)
    c: Horizontal(g14)
    c: Horizontal(g16)
    c: Vertical(g15)
    c: Coincident(g17,g18)
    c: Coincident(g18,g19)
    c: Horizontal(g18)
    c: Vertical(g17)
    c: Vertical(g19)
    c: Equal(g15,g18)
    c: Coincident(g16,g17)
    c: Equal(g17,g16)
    c: Coincident(g19,g14)
    c: Coincident(g20,g21)
    c: Coincident(g21,g22)
    c: Horizontal(g20)
    c: Horizontal(g22)
    c: Vertical(g21)
    c: Coincident(g23,g24)
    c: Coincident(g24,g25)
    c: Horizontal(g24)
    c: Vertical(g23)
    c: Vertical(g25)
    c: Equal(g21,g24)
    c: Coincident(g22,g23)
    c: Equal(g23,g22)
    c: Coincident(g25,g20)
FEATURE [PartDesign::Pad] Pad031
  BaseFeature = -> Pocket031
  Length = 3
  Length2 = 100
  Profile = -> Sketch063
  Refine = true
  Type = 0
FEATURE [PartDesign::Body] Body014  label="tapa-caja-CCS811"
  Group = -> [Sketch060,Pad029,Sketch061,Pad030,Sketch062,Pocket031,Sketch063,Pad031]
  Origin = -> Origin014
  Tip = -> Pad031
FEATURE [Part::FeaturePython] Clone029  label="tapa-caja-CCS812-e"  # Draft clone (typed FeaturePython)
  AttacherType = Attacher::AttachEngine3D
  Fuse = false
  Objects = -> [Pad031]
  Placement = pos=(-243,207.5,372) rot=(0.707107,0.707107,0;3.14159rad)
  Scale = (1,1,1)
FEATURE [Sketcher::SketchObject] Sketch064
  ExternalGeometry = -> [Pocket024]
  MapMode = 5
  Placement = pos=(0,0,0) rot=(1,0,0;3.14159rad)
  Support = -> [Pocket024]
  sketch-geometry (1):
    g0: Circle CenterX=288 CenterY=-69.55 CenterZ=0 NormalX=0 NormalY=0 NormalZ=1 AngleXU=0 Radius=1.5
  constraints (3):
    c: Diameter(g0) = 3
    c: DistanceX(g0,g-3) = 32
    c: DistanceY(g0,g-3) = 12
FEATURE [PartDesign::Pocket] Pocket032
  BaseFeature = -> Pocket024
  Length = 5
  Length2 = 100
  Profile = -> Sketch064
  Refine = true
  Type = 0
FEATURE [PartDesign::Body] Body007  label="tapa-posterior-sensores"
  Group = -> [Sketch023,Pad014,Sketch024,Pad015,Sketch025,Pad016,Sketch026,Sketch027,Pocket009,Pad017,Sketch042,Pocket017,Sketch043,Pocket018,Sketch044,Pocket019,Sketch052,Pocket024,Sketch064,Pocket032]
  Origin = -> Origin007
  Tip = -> Pocket032
FEATURE [Part::FeaturePython] Clone030  label="tapa-posterior-sensores-e"  # Draft clone (typed FeaturePython)
  AttacherType = Attacher::AttachEngine3D
  Fuse = false
  Objects = -> [Pocket032]
  Placement = pos=(-50,145.5,52) rot=(0.707107,0,0.707107;3.14159rad)
  Scale = (1,1,1)
FEATURE [Mesh::Feature] NODE_MCU_con_Shield  label="NODE-MCU-con-Shield"
  Placement = pos=(-109,-15,36) rot=(-0.57735,-0.57735,0.57735;2.0944rad)
FEATURE [App::DocumentObjectGroup] Grupo001  label="electronica"
  Group = -> [hub,Arduino,amplificador_2W,NODE_MCU_con_Shield]
FEATURE [Sketcher::SketchObject] Sketch065
  MapMode = 5
  Placement = pos=(-107.57,0,0) rot=(0.57735,-0.57735,-0.57735;2.0944rad)
  Support = -> [Pocket014]
  sketch-geometry (4):
    g0: Circle CenterX=-11.9927 CenterY=46.0682 CenterZ=0 NormalX=0 NormalY=0 NormalZ=1 AngleXU=0 Radius=2
    g1: Circle CenterX=39.721 CenterY=45.8521 CenterZ=0 NormalX=0 NormalY=0 NormalZ=1 AngleXU=0 Radius=2
    g2: Circle CenterX=-11.9091 CenterY=21.0235 CenterZ=0 NormalX=0 NormalY=0 NormalZ=1 AngleXU=0 Radius=2
    g3: Circle CenterX=39.8265 CenterY=21.0669 CenterZ=0 NormalX=0 NormalY=0 NormalZ=1 AngleXU=0 Radius=2
  constraints (4):
    c: Equal(g3,g2)
    c: Equal(g2,g0)
    c: Equal(g0,g1)
    c: Radius(g1) = 2
FEATURE [PartDesign::Pocket] Pocket033
  BaseFeature = -> Pocket014
  Length = 5
  Length2 = 100
  Profile = -> Sketch065
  Refine = true
  Type = 0
FEATURE [PartDesign::Body] Body008  label="Base"
  Group = -> [Sketch030,Pad018,Sketch031,Pad019,Sketch032,Pocket012,Sketch033,Pocket013,Sketch034,Pocket014,Sketch065,Pocket033]
  Origin = -> Origin008
  Tip = -> Pocket033
FEATURE [App::DocumentObjectGroup] Grupo  label="Diseño"
  Group = -> [Body,Body001,Body002,Body003,Body004,Body005,Body006,Body007,Body008,Body009,Body010,Body011,Body013,Body014]
FEATURE [Part::FeaturePython] Clone031  label="base-e"  # Draft clone (typed FeaturePython)
  AttacherType = Attacher::AttachEngine3D
  Fuse = false
  Objects = -> [Pocket033]
  Placement = pos=(50,50,-67) rot=(0.707107,0,-0.707107;3.14159rad)
  Scale = (1,1,1)
FEATURE [Part::FeaturePython] Clone032  label="tapa-posterior-base-e"  # Draft clone (typed FeaturePython)
  AttacherType = Attacher::AttachEngine3D
  Fuse = false
  Objects = -> [Pocket015]
  Placement = pos=(-52,-63,-68) rot=(0,1,0;1.5708rad)
  Scale = (1,1,1)
FEATURE [App::DocumentObjectGroup] Grupo002  label="impresion"
  Group = -> [Clone,Clone006,Clone012,Clone013,Clone015,Clone017,Clone019,Clone021,Clone022,Clone023,Clone025,Clone027,Clone029,Clone030,Clone031,Clone032]
